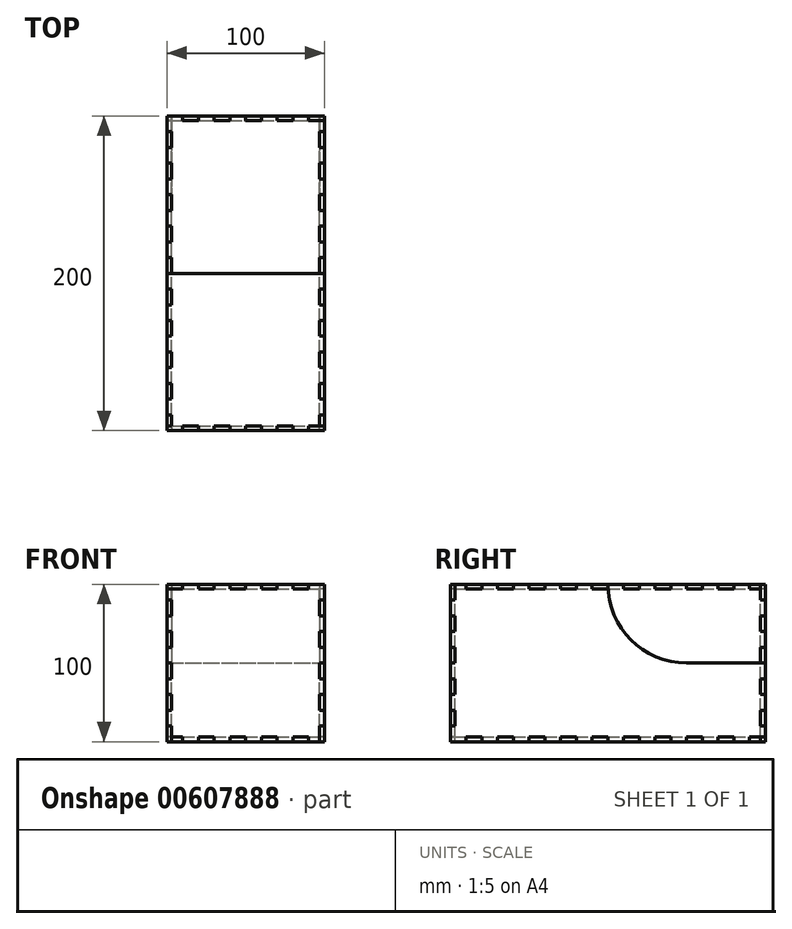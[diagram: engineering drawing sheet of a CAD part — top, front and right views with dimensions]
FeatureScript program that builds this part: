
annotation { "Feature Type Name" : "Feature", "Feature Type Description" : "" }
export const myFeature = defineFeature(function(context is Context, id is Id, definition is map)
    precondition{}
    {
        {
            var Q0;
            Q0=qCreatedBy(makeId("Right.planeOp"),FACE);
            var sketch = newSketch(context, id + "F0", { "sketchPlane" : qUnion([Q0])});
            skLineSegment(sketch, "E0.bottom", {"start": v(3, 0) * mm, "end": v(10, 0) * mm});
            skLineSegment(sketch, "E0.top", {"start": v(0, -100) * mm, "end": v(10, -100) * mm});
            skLineSegment(sketch, "E0.left", {"start": v(0, -10) * mm, "end": v(0, -20) * mm});
            skLineSegment(sketch, "E0.right", {"start": v(200, -10) * mm, "end": v(200, -20) * mm});
            skArc(sketch, "E1", {"start": v(100, 0) * mm, "mid": v(114.64, -35.36) * mm, "end": v(150, -50) * mm});
            skLineSegment(sketch, "E2", {"start": v(200, -50) * mm, "end": v(150, -50) * mm});
            skLineSegment(sketch, "E3.bottom", {"start": v(0, -90) * mm, "end": v(3, -90) * mm});
            skLineSegment(sketch, "E3.top", {"start": v(0, -80) * mm, "end": v(3, -80) * mm});
            skLineSegment(sketch, "E3.right", {"start": v(3, -90) * mm, "end": v(3, -80) * mm});
            skLineSegment(sketch, "E4.trimOffspring", {"start": v(0, -90) * mm, "end": v(0, -100) * mm});
            skLineSegment(sketch, "E5.0.1.0", {"start": v(0, -70) * mm, "end": v(3, -70) * mm});
            skLineSegment(sketch, "E5.0.1.1", {"start": v(3, -70) * mm, "end": v(3, -60) * mm});
            skLineSegment(sketch, "E5.0.1.2", {"start": v(0, -60) * mm, "end": v(3, -60) * mm});
            skLineSegment(sketch, "E5.0.2.0", {"start": v(0, -50) * mm, "end": v(3, -50) * mm});
            skLineSegment(sketch, "E5.0.2.1", {"start": v(3, -50) * mm, "end": v(3, -40) * mm});
            skLineSegment(sketch, "E5.0.2.2", {"start": v(0, -40) * mm, "end": v(3, -40) * mm});
            skLineSegment(sketch, "E5.0.3.0", {"start": v(0, -30) * mm, "end": v(3, -30) * mm});
            skLineSegment(sketch, "E5.0.3.1", {"start": v(3, -30) * mm, "end": v(3, -20) * mm});
            skLineSegment(sketch, "E5.0.3.2", {"start": v(0, -20) * mm, "end": v(3, -20) * mm});
            skLineSegment(sketch, "E5.0.4.0", {"start": v(0, -10) * mm, "end": v(3, -10) * mm});
            skLineSegment(sketch, "E5.0.4.1", {"start": v(3, -10) * mm, "end": v(3, 0) * mm});
            skLineSegment(sketch, "E5.direction1", {"start": v(0, -90) * mm, "end": v(25, -90) * mm, "construction": true});
            skLineSegment(sketch, "E5.direction2", {"start": v(0, -90) * mm, "end": v(0, -70) * mm, "construction": true});
            skLineSegment(sketch, "E6.trimOffspring", {"start": v(0, -30) * mm, "end": v(0, -40) * mm});
            skLineSegment(sketch, "E7.trimOffspring", {"start": v(0, -50) * mm, "end": v(0, -60) * mm});
            skLineSegment(sketch, "E8.trimOffspring", {"start": v(0, -70) * mm, "end": v(0, -80) * mm});
            skLineSegment(sketch, "E9.top", {"start": v(10, -97) * mm, "end": v(20, -97) * mm});
            skLineSegment(sketch, "E9.left", {"start": v(10, -100) * mm, "end": v(10, -97) * mm});
            skLineSegment(sketch, "E9.right", {"start": v(20, -100) * mm, "end": v(20, -97) * mm});
            skLineSegment(sketch, "E10.trimOffspring", {"start": v(20, -100) * mm, "end": v(30, -100) * mm});
            skLineSegment(sketch, "E11.1.0.0", {"start": v(30, -97) * mm, "end": v(40, -97) * mm});
            skLineSegment(sketch, "E11.1.0.1", {"start": v(40, -100) * mm, "end": v(40, -97) * mm});
            skLineSegment(sketch, "E11.1.0.3", {"start": v(30, -100) * mm, "end": v(30, -97) * mm});
            skLineSegment(sketch, "E11.2.0.0", {"start": v(50, -97) * mm, "end": v(60, -97) * mm});
            skLineSegment(sketch, "E11.2.0.1", {"start": v(60, -100) * mm, "end": v(60, -97) * mm});
            skLineSegment(sketch, "E11.2.0.2", {"start": v(40, -100) * mm, "end": v(50, -100) * mm});
            skLineSegment(sketch, "E11.2.0.3", {"start": v(50, -100) * mm, "end": v(50, -97) * mm});
            skLineSegment(sketch, "E11.3.0.0", {"start": v(70, -97) * mm, "end": v(80, -97) * mm});
            skLineSegment(sketch, "E11.3.0.1", {"start": v(80, -100) * mm, "end": v(80, -97) * mm});
            skLineSegment(sketch, "E11.3.0.2", {"start": v(60, -100) * mm, "end": v(70, -100) * mm});
            skLineSegment(sketch, "E11.3.0.3", {"start": v(70, -100) * mm, "end": v(70, -97) * mm});
            skLineSegment(sketch, "E11.4.0.0", {"start": v(90, -97) * mm, "end": v(100, -97) * mm});
            skLineSegment(sketch, "E11.4.0.1", {"start": v(100, -100) * mm, "end": v(100, -97) * mm});
            skLineSegment(sketch, "E11.4.0.2", {"start": v(80, -100) * mm, "end": v(90, -100) * mm});
            skLineSegment(sketch, "E11.4.0.3", {"start": v(90, -100) * mm, "end": v(90, -97) * mm});
            skLineSegment(sketch, "E11.5.0.0", {"start": v(110, -97) * mm, "end": v(120, -97) * mm});
            skLineSegment(sketch, "E11.5.0.1", {"start": v(120, -100) * mm, "end": v(120, -97) * mm});
            skLineSegment(sketch, "E11.5.0.2", {"start": v(100, -100) * mm, "end": v(110, -100) * mm});
            skLineSegment(sketch, "E11.5.0.3", {"start": v(110, -100) * mm, "end": v(110, -97) * mm});
            skLineSegment(sketch, "E11.6.0.0", {"start": v(130, -97) * mm, "end": v(140, -97) * mm});
            skLineSegment(sketch, "E11.6.0.1", {"start": v(140, -100) * mm, "end": v(140, -97) * mm});
            skLineSegment(sketch, "E11.6.0.2", {"start": v(120, -100) * mm, "end": v(130, -100) * mm});
            skLineSegment(sketch, "E11.6.0.3", {"start": v(130, -100) * mm, "end": v(130, -97) * mm});
            skLineSegment(sketch, "E11.7.0.0", {"start": v(150, -97) * mm, "end": v(160, -97) * mm});
            skLineSegment(sketch, "E11.7.0.1", {"start": v(160, -100) * mm, "end": v(160, -97) * mm});
            skLineSegment(sketch, "E11.7.0.2", {"start": v(140, -100) * mm, "end": v(150, -100) * mm});
            skLineSegment(sketch, "E11.7.0.3", {"start": v(150, -100) * mm, "end": v(150, -97) * mm});
            skLineSegment(sketch, "E11.8.0.0", {"start": v(170, -97) * mm, "end": v(180, -97) * mm});
            skLineSegment(sketch, "E11.8.0.1", {"start": v(180, -100) * mm, "end": v(180, -97) * mm});
            skLineSegment(sketch, "E11.8.0.2", {"start": v(160, -100) * mm, "end": v(170, -100) * mm});
            skLineSegment(sketch, "E11.8.0.3", {"start": v(170, -100) * mm, "end": v(170, -97) * mm});
            skLineSegment(sketch, "E11.9.0.0", {"start": v(190, -97) * mm, "end": v(200, -97) * mm});
            skLineSegment(sketch, "E11.9.0.2", {"start": v(180, -100) * mm, "end": v(190, -100) * mm});
            skLineSegment(sketch, "E11.9.0.3", {"start": v(190, -100) * mm, "end": v(190, -97) * mm});
            skLineSegment(sketch, "E11.direction1", {"start": v(0, -100) * mm, "end": v(20, -100) * mm, "construction": true});
            skLineSegment(sketch, "E12.top", {"start": v(197, -10) * mm, "end": v(200, -10) * mm});
            skLineSegment(sketch, "E12.left", {"start": v(197, -3) * mm, "end": v(197, -10) * mm});
            skLineSegment(sketch, "E13.0.1.1", {"start": v(197, -20) * mm, "end": v(197, -30) * mm});
            skLineSegment(sketch, "E13.0.1.2", {"start": v(197, -30) * mm, "end": v(200, -30) * mm});
            skLineSegment(sketch, "E13.0.1.3", {"start": v(197, -20) * mm, "end": v(200, -20) * mm});
            skLineSegment(sketch, "E13.0.2.1", {"start": v(197, -40) * mm, "end": v(197, -50) * mm});
            skLineSegment(sketch, "E13.0.2.2", {"start": v(197, -50) * mm, "end": v(200, -50) * mm});
            skLineSegment(sketch, "E13.0.2.3", {"start": v(197, -40) * mm, "end": v(200, -40) * mm});
            skLineSegment(sketch, "E13.0.3.1", {"start": v(197, -60) * mm, "end": v(197, -70) * mm});
            skLineSegment(sketch, "E13.0.3.2", {"start": v(197, -70) * mm, "end": v(200, -70) * mm});
            skLineSegment(sketch, "E13.0.3.3", {"start": v(197, -60) * mm, "end": v(200, -60) * mm});
            skLineSegment(sketch, "E13.0.4.1", {"start": v(197, -80) * mm, "end": v(197, -90) * mm});
            skLineSegment(sketch, "E13.0.4.2", {"start": v(197, -90) * mm, "end": v(200, -90) * mm});
            skLineSegment(sketch, "E13.0.4.3", {"start": v(197, -80) * mm, "end": v(200, -80) * mm});
            skLineSegment(sketch, "E13.direction1", {"start": v(197, -10) * mm, "end": v(222, -10) * mm, "construction": true});
            skLineSegment(sketch, "E13.direction2", {"start": v(197, -10) * mm, "end": v(197, -30) * mm, "construction": true});
            skLineSegment(sketch, "E14.trimOffspring", {"start": v(200, -90) * mm, "end": v(200, -97) * mm});
            skLineSegment(sketch, "E15.trimOffspring", {"start": v(200, -70) * mm, "end": v(200, -80) * mm});
            skLineSegment(sketch, "E16.trimOffspring", {"start": v(200, -50) * mm, "end": v(200, -60) * mm});
            skLineSegment(sketch, "E17.trimOffspring", {"start": v(200, -30) * mm, "end": v(200, -40) * mm});
            skLineSegment(sketch, "E18.top", {"start": v(10, -3) * mm, "end": v(20, -3) * mm});
            skLineSegment(sketch, "E18.left", {"start": v(10, 0) * mm, "end": v(10, -3) * mm});
            skLineSegment(sketch, "E18.right", {"start": v(20, 0) * mm, "end": v(20, -3) * mm});
            skLineSegment(sketch, "E19.trimOffspring", {"start": v(20, 0) * mm, "end": v(30, 0) * mm});
            skLineSegment(sketch, "E20.1.0.0", {"start": v(30, -3) * mm, "end": v(40, -3) * mm});
            skLineSegment(sketch, "E20.1.0.1", {"start": v(40, 0) * mm, "end": v(40, -3) * mm});
            skLineSegment(sketch, "E20.1.0.2", {"start": v(30, 0) * mm, "end": v(30, -3) * mm});
            skLineSegment(sketch, "E20.2.0.0", {"start": v(50, -3) * mm, "end": v(60, -3) * mm});
            skLineSegment(sketch, "E20.2.0.1", {"start": v(60, 0) * mm, "end": v(60, -3) * mm});
            skLineSegment(sketch, "E20.2.0.2", {"start": v(50, 0) * mm, "end": v(50, -3) * mm});
            skLineSegment(sketch, "E20.3.0.0", {"start": v(70, -3) * mm, "end": v(80, -3) * mm});
            skLineSegment(sketch, "E20.3.0.1", {"start": v(80, 0) * mm, "end": v(80, -3) * mm});
            skLineSegment(sketch, "E20.3.0.2", {"start": v(70, 0) * mm, "end": v(70, -3) * mm});
            skLineSegment(sketch, "E20.4.0.0", {"start": v(90, -3) * mm, "end": v(100, -3) * mm});
            skLineSegment(sketch, "E20.4.0.1", {"start": v(100, 0) * mm, "end": v(100, -3) * mm});
            skLineSegment(sketch, "E20.4.0.2", {"start": v(90, 0) * mm, "end": v(90, -3) * mm});
            skLineSegment(sketch, "E20.5.0.0", {"start": v(110, -3) * mm, "end": v(120, -3) * mm});
            skLineSegment(sketch, "E20.5.0.1", {"start": v(120, 0) * mm, "end": v(120, -3) * mm});
            skLineSegment(sketch, "E20.5.0.2", {"start": v(110, 0) * mm, "end": v(110, -3) * mm});
            skLineSegment(sketch, "E20.6.0.0", {"start": v(130, -3) * mm, "end": v(140, -3) * mm});
            skLineSegment(sketch, "E20.6.0.1", {"start": v(140, 0) * mm, "end": v(140, -3) * mm});
            skLineSegment(sketch, "E20.6.0.2", {"start": v(130, 0) * mm, "end": v(130, -3) * mm});
            skLineSegment(sketch, "E20.7.0.0", {"start": v(150, -3) * mm, "end": v(160, -3) * mm});
            skLineSegment(sketch, "E20.7.0.1", {"start": v(160, 0) * mm, "end": v(160, -3) * mm});
            skLineSegment(sketch, "E20.7.0.2", {"start": v(150, 0) * mm, "end": v(150, -3) * mm});
            skLineSegment(sketch, "E20.8.0.0", {"start": v(170, -3) * mm, "end": v(180, -3) * mm});
            skLineSegment(sketch, "E20.8.0.1", {"start": v(180, 0) * mm, "end": v(180, -3) * mm});
            skLineSegment(sketch, "E20.8.0.2", {"start": v(170, 0) * mm, "end": v(170, -3) * mm});
            skLineSegment(sketch, "E20.9.0.0", {"start": v(190, -3) * mm, "end": v(200, -3) * mm});
            skLineSegment(sketch, "E20.9.0.2", {"start": v(190, 0) * mm, "end": v(190, -3) * mm});
            skLineSegment(sketch, "E20.direction1", {"start": v(10, -3) * mm, "end": v(30, -3) * mm, "construction": true});
            skLineSegment(sketch, "E21.trimOffspring", {"start": v(40, 0) * mm, "end": v(50, 0) * mm});
            skLineSegment(sketch, "E22.trimOffspring", {"start": v(60, 0) * mm, "end": v(70, 0) * mm});
            skLineSegment(sketch, "E23.trimOffspring", {"start": v(80, 0) * mm, "end": v(90, 0) * mm});
            skLineSegment(sketch, "E24.trimOffspring", {"start": v(100, 0) * mm, "end": v(110, 0) * mm});
            skLineSegment(sketch, "E25.trimOffspring", {"start": v(120, 0) * mm, "end": v(130, 0) * mm});
            skLineSegment(sketch, "E26.trimOffspring", {"start": v(140, 0) * mm, "end": v(150, 0) * mm});
            skLineSegment(sketch, "E27.trimOffspring", {"start": v(160, 0) * mm, "end": v(170, 0) * mm});
            skLineSegment(sketch, "E28.trimOffspring", {"start": v(180, 0) * mm, "end": v(190, 0) * mm});
            skSolve(sketch);
        }
        {
            var Q0;
            Q0=makeQuery(id+"F0.imprint","IMPRINT",FACE,{"disambiguationData":[TD([[makeQuery(id+"F0.imprint","IMPRINT",EDGE,{"derivedFrom":sQuery(id+"F0.wireOp",EDGE,"E0.bottom")}),-1.0]])]});
            extrude(context, id + "F1", {"entities" : qUnion([Q0]), "depth" : 3 * mm, "offsetDistance" : 25 * mm});
        }
        {
            var Q0;
            Q0=makeQuery(id+"F0.imprint","IMPRINT",FACE,{"disambiguationData":[TD([[makeQuery(id+"F0.imprint","IMPRINT",EDGE,{"derivedFrom":sQuery(id+"F0.wireOp",EDGE,"E0.right")}),-1.0]])]});
            extrude(context, id + "F2", {"entities" : qUnion([Q0]), "depth" : 3 * mm, "offsetDistance" : 25 * mm});
        }
        {
            var Q0;
            Q0=qCreatedBy(makeId("Front.planeOp"),FACE);
            var sketch = newSketch(context, id + "F3", { "sketchPlane" : qUnion([Q0])});
            skLineSegment(sketch, "E29.bottom", {"start": v(3, 0) * mm, "end": v(-7, 0) * mm});
            skLineSegment(sketch, "E29.top", {"start": v(3, -100) * mm, "end": v(-7, -100) * mm});
            skLineSegment(sketch, "E29.left", {"start": v(3, 0) * mm, "end": v(3, -100) * mm});
            skLineSegment(sketch, "E29.right", {"start": v(-97, -3) * mm, "end": v(-97, -100) * mm});
            skLineSegment(sketch, "E30.top", {"start": v(-97, -3) * mm, "end": v(-87, -3) * mm});
            skLineSegment(sketch, "E30.right", {"start": v(-87, 0) * mm, "end": v(-87, -3) * mm});
            skLineSegment(sketch, "E31.top", {"start": v(-97, -97) * mm, "end": v(-87, -97) * mm});
            skLineSegment(sketch, "E31.left", {"start": v(-97, -100) * mm, "end": v(-97, -97) * mm});
            skLineSegment(sketch, "E31.right", {"start": v(-87, -100) * mm, "end": v(-87, -97) * mm});
            skLineSegment(sketch, "E32.1.0.0", {"start": v(-67, 0) * mm, "end": v(-67, -3) * mm});
            skLineSegment(sketch, "E32.1.0.1", {"start": v(-77, 0) * mm, "end": v(-77, -3) * mm});
            skLineSegment(sketch, "E32.1.0.2", {"start": v(-77, -3) * mm, "end": v(-67, -3) * mm});
            skLineSegment(sketch, "E32.2.0.0", {"start": v(-47, 0) * mm, "end": v(-47, -3) * mm});
            skLineSegment(sketch, "E32.2.0.1", {"start": v(-57, 0) * mm, "end": v(-57, -3) * mm});
            skLineSegment(sketch, "E32.2.0.2", {"start": v(-57, -3) * mm, "end": v(-47, -3) * mm});
            skLineSegment(sketch, "E32.3.0.0", {"start": v(-27, 0) * mm, "end": v(-27, -3) * mm});
            skLineSegment(sketch, "E32.3.0.1", {"start": v(-37, 0) * mm, "end": v(-37, -3) * mm});
            skLineSegment(sketch, "E32.3.0.2", {"start": v(-37, -3) * mm, "end": v(-27, -3) * mm});
            skLineSegment(sketch, "E32.4.0.0", {"start": v(-7, 0) * mm, "end": v(-7, -3) * mm});
            skLineSegment(sketch, "E32.4.0.1", {"start": v(-17, 0) * mm, "end": v(-17, -3) * mm});
            skLineSegment(sketch, "E32.4.0.2", {"start": v(-17, -3) * mm, "end": v(-7, -3) * mm});
            skLineSegment(sketch, "E32.direction1", {"start": v(-97, -3) * mm, "end": v(-77, -3) * mm, "construction": true});
            skLineSegment(sketch, "E33.1.0.1", {"start": v(-77, -97) * mm, "end": v(-67, -97) * mm});
            skLineSegment(sketch, "E33.1.0.2", {"start": v(-77, -100) * mm, "end": v(-77, -97) * mm});
            skLineSegment(sketch, "E33.1.0.3", {"start": v(-67, -100) * mm, "end": v(-67, -97) * mm});
            skLineSegment(sketch, "E33.2.0.1", {"start": v(-57, -97) * mm, "end": v(-47, -97) * mm});
            skLineSegment(sketch, "E33.2.0.2", {"start": v(-57, -100) * mm, "end": v(-57, -97) * mm});
            skLineSegment(sketch, "E33.2.0.3", {"start": v(-47, -100) * mm, "end": v(-47, -97) * mm});
            skLineSegment(sketch, "E33.3.0.1", {"start": v(-37, -97) * mm, "end": v(-27, -97) * mm});
            skLineSegment(sketch, "E33.3.0.2", {"start": v(-37, -100) * mm, "end": v(-37, -97) * mm});
            skLineSegment(sketch, "E33.3.0.3", {"start": v(-27, -100) * mm, "end": v(-27, -97) * mm});
            skLineSegment(sketch, "E33.4.0.1", {"start": v(-17, -97) * mm, "end": v(-7, -97) * mm});
            skLineSegment(sketch, "E33.4.0.2", {"start": v(-17, -100) * mm, "end": v(-17, -97) * mm});
            skLineSegment(sketch, "E33.4.0.3", {"start": v(-7, -100) * mm, "end": v(-7, -97) * mm});
            skLineSegment(sketch, "E33.direction1", {"start": v(-87, -100) * mm, "end": v(-77, -100) * mm, "construction": true});
            skLineSegment(sketch, "E34.trimOffspring", {"start": v(-77, 0) * mm, "end": v(-87, 0) * mm});
            skLineSegment(sketch, "E35.trimOffspring", {"start": v(-57, 0) * mm, "end": v(-67, 0) * mm});
            skLineSegment(sketch, "E36.trimOffspring", {"start": v(-37, 0) * mm, "end": v(-47, 0) * mm});
            skLineSegment(sketch, "E37.trimOffspring", {"start": v(-17, 0) * mm, "end": v(-27, 0) * mm});
            skLineSegment(sketch, "E38.trimOffspring", {"start": v(-17, -100) * mm, "end": v(-27, -100) * mm});
            skLineSegment(sketch, "E39.trimOffspring", {"start": v(-37, -100) * mm, "end": v(-47, -100) * mm});
            skLineSegment(sketch, "E40.trimOffspring", {"start": v(-57, -100) * mm, "end": v(-67, -100) * mm});
            skLineSegment(sketch, "E41.trimOffspring", {"start": v(-77, -100) * mm, "end": v(-87, -100) * mm});
            skLineSegment(sketch, "E42", {"start": v(-97, -50) * mm, "end": v(3, -50) * mm});
            skSolve(sketch);
        }
        {
            var Q0;
            Q0=makeQuery(id+"F1.opExtrude","SWEPT_BODY",BODY,{"disambiguationData":[OSD([sQuery(id+"F0.wireOp",EDGE,"E0.bottom"),sQuery(id+"F0.wireOp",EDGE,"E0.top"),sQuery(id+"F0.wireOp",EDGE,"E0.left"),sQuery(id+"F0.wireOp",EDGE,"E1"),sQuery(id+"F0.wireOp",EDGE,"E2"),sQuery(id+"F0.wireOp",EDGE,"E3.bottom"),sQuery(id+"F0.wireOp",EDGE,"E3.top"),sQuery(id+"F0.wireOp",EDGE,"E3.right"),sQuery(id+"F0.wireOp",EDGE,"E4.trimOffspring"),sQuery(id+"F0.wireOp",EDGE,"E5.0.1.0"),sQuery(id+"F0.wireOp",EDGE,"E5.0.1.1"),sQuery(id+"F0.wireOp",EDGE,"E5.0.1.2"),sQuery(id+"F0.wireOp",EDGE,"E5.0.2.0"),sQuery(id+"F0.wireOp",EDGE,"E5.0.2.1"),sQuery(id+"F0.wireOp",EDGE,"E5.0.2.2"),sQuery(id+"F0.wireOp",EDGE,"E5.0.3.0"),sQuery(id+"F0.wireOp",EDGE,"E5.0.3.1"),sQuery(id+"F0.wireOp",EDGE,"E5.0.3.2"),sQuery(id+"F0.wireOp",EDGE,"E5.0.4.0"),sQuery(id+"F0.wireOp",EDGE,"E5.0.4.1"),sQuery(id+"F0.wireOp",EDGE,"E6.trimOffspring"),sQuery(id+"F0.wireOp",EDGE,"E7.trimOffspring"),sQuery(id+"F0.wireOp",EDGE,"E8.trimOffspring"),sQuery(id+"F0.wireOp",EDGE,"E9.top"),sQuery(id+"F0.wireOp",EDGE,"E9.left"),sQuery(id+"F0.wireOp",EDGE,"E9.right"),sQuery(id+"F0.wireOp",EDGE,"E11.1.0.0"),sQuery(id+"F0.wireOp",EDGE,"E11.1.0.1"),sQuery(id+"F0.wireOp",EDGE,"E10.trimOffspring"),sQuery(id+"F0.wireOp",EDGE,"E11.1.0.3"),sQuery(id+"F0.wireOp",EDGE,"E11.2.0.0"),sQuery(id+"F0.wireOp",EDGE,"E11.2.0.1"),sQuery(id+"F0.wireOp",EDGE,"E11.2.0.3"),sQuery(id+"F0.wireOp",EDGE,"E11.3.0.0"),sQuery(id+"F0.wireOp",EDGE,"E11.3.0.1"),sQuery(id+"F0.wireOp",EDGE,"E11.3.0.3"),sQuery(id+"F0.wireOp",EDGE,"E11.4.0.0"),sQuery(id+"F0.wireOp",EDGE,"E11.4.0.1"),sQuery(id+"F0.wireOp",EDGE,"E11.4.0.3"),sQuery(id+"F0.wireOp",EDGE,"E11.5.0.0"),sQuery(id+"F0.wireOp",EDGE,"E11.5.0.1"),sQuery(id+"F0.wireOp",EDGE,"E11.5.0.3"),sQuery(id+"F0.wireOp",EDGE,"E11.6.0.0"),sQuery(id+"F0.wireOp",EDGE,"E11.6.0.1"),sQuery(id+"F0.wireOp",EDGE,"E11.6.0.3"),sQuery(id+"F0.wireOp",EDGE,"E11.7.0.0"),sQuery(id+"F0.wireOp",EDGE,"E11.7.0.1"),sQuery(id+"F0.wireOp",EDGE,"E11.7.0.3"),sQuery(id+"F0.wireOp",EDGE,"E11.8.0.0"),sQuery(id+"F0.wireOp",EDGE,"E11.8.0.1"),sQuery(id+"F0.wireOp",EDGE,"E11.8.0.3"),sQuery(id+"F0.wireOp",EDGE,"E11.9.0.0"),sQuery(id+"F0.wireOp",EDGE,"E11.9.0.3"),sQuery(id+"F0.wireOp",EDGE,"E11.2.0.2"),sQuery(id+"F0.wireOp",EDGE,"E11.3.0.2"),sQuery(id+"F0.wireOp",EDGE,"E11.4.0.2"),sQuery(id+"F0.wireOp",EDGE,"E11.5.0.2"),sQuery(id+"F0.wireOp",EDGE,"E11.6.0.2"),sQuery(id+"F0.wireOp",EDGE,"E11.7.0.2"),sQuery(id+"F0.wireOp",EDGE,"E11.8.0.2"),sQuery(id+"F0.wireOp",EDGE,"E11.9.0.2"),sQuery(id+"F0.wireOp",EDGE,"E13.0.2.2"),sQuery(id+"F0.wireOp",EDGE,"E13.0.3.1"),sQuery(id+"F0.wireOp",EDGE,"E13.0.3.2"),sQuery(id+"F0.wireOp",EDGE,"E13.0.3.3"),sQuery(id+"F0.wireOp",EDGE,"E13.0.4.1"),sQuery(id+"F0.wireOp",EDGE,"E13.0.4.2"),sQuery(id+"F0.wireOp",EDGE,"E13.0.4.3"),sQuery(id+"F0.wireOp",EDGE,"E14.trimOffspring"),sQuery(id+"F0.wireOp",EDGE,"E15.trimOffspring"),sQuery(id+"F0.wireOp",EDGE,"E16.trimOffspring"),sQuery(id+"F0.wireOp",EDGE,"E18.top"),sQuery(id+"F0.wireOp",EDGE,"E18.left"),sQuery(id+"F0.wireOp",EDGE,"E18.right"),sQuery(id+"F0.wireOp",EDGE,"E19.trimOffspring"),sQuery(id+"F0.wireOp",EDGE,"E20.1.0.0"),sQuery(id+"F0.wireOp",EDGE,"E20.1.0.1"),sQuery(id+"F0.wireOp",EDGE,"E20.1.0.2"),sQuery(id+"F0.wireOp",EDGE,"E20.2.0.0"),sQuery(id+"F0.wireOp",EDGE,"E20.2.0.1"),sQuery(id+"F0.wireOp",EDGE,"E20.2.0.2"),sQuery(id+"F0.wireOp",EDGE,"E20.3.0.0"),sQuery(id+"F0.wireOp",EDGE,"E20.3.0.1"),sQuery(id+"F0.wireOp",EDGE,"E20.3.0.2"),sQuery(id+"F0.wireOp",EDGE,"E20.4.0.0"),sQuery(id+"F0.wireOp",EDGE,"E20.4.0.1"),sQuery(id+"F0.wireOp",EDGE,"E20.4.0.2"),sQuery(id+"F0.wireOp",EDGE,"E21.trimOffspring"),sQuery(id+"F0.wireOp",EDGE,"E22.trimOffspring"),sQuery(id+"F0.wireOp",EDGE,"E23.trimOffspring")])]});
            transform(context, id + "F4", {"entities" : qUnion([Q0]), "transformType" : TransformType.TRANSLATION_3D, "dx" : -97 * mm, "dy" : 0 * mm, "dz" : 0 * mm, "makeCopy" : true});
        }
        {
            var Q0;
            Q0=makeQuery(id+"F2.opExtrude","SWEPT_BODY",BODY,{"disambiguationData":[OSD([sQuery(id+"F0.wireOp",EDGE,"E0.right"),sQuery(id+"F0.wireOp",EDGE,"E1"),sQuery(id+"F0.wireOp",EDGE,"E2"),sQuery(id+"F0.wireOp",EDGE,"E12.top"),sQuery(id+"F0.wireOp",EDGE,"E12.left"),sQuery(id+"F0.wireOp",EDGE,"E13.0.1.1"),sQuery(id+"F0.wireOp",EDGE,"E13.0.1.2"),sQuery(id+"F0.wireOp",EDGE,"E13.0.1.3"),sQuery(id+"F0.wireOp",EDGE,"E13.0.2.1"),sQuery(id+"F0.wireOp",EDGE,"E13.0.2.3"),sQuery(id+"F0.wireOp",EDGE,"E17.trimOffspring"),sQuery(id+"F0.wireOp",EDGE,"E20.5.0.0"),sQuery(id+"F0.wireOp",EDGE,"E20.5.0.1"),sQuery(id+"F0.wireOp",EDGE,"E20.5.0.2"),sQuery(id+"F0.wireOp",EDGE,"E20.6.0.0"),sQuery(id+"F0.wireOp",EDGE,"E20.6.0.1"),sQuery(id+"F0.wireOp",EDGE,"E20.6.0.2"),sQuery(id+"F0.wireOp",EDGE,"E20.7.0.0"),sQuery(id+"F0.wireOp",EDGE,"E20.7.0.1"),sQuery(id+"F0.wireOp",EDGE,"E20.7.0.2"),sQuery(id+"F0.wireOp",EDGE,"E20.8.0.0"),sQuery(id+"F0.wireOp",EDGE,"E20.8.0.1"),sQuery(id+"F0.wireOp",EDGE,"E20.8.0.2"),sQuery(id+"F0.wireOp",EDGE,"E20.9.0.0"),sQuery(id+"F0.wireOp",EDGE,"E20.9.0.2"),sQuery(id+"F0.wireOp",EDGE,"E24.trimOffspring"),sQuery(id+"F0.wireOp",EDGE,"E25.trimOffspring"),sQuery(id+"F0.wireOp",EDGE,"E26.trimOffspring"),sQuery(id+"F0.wireOp",EDGE,"E27.trimOffspring"),sQuery(id+"F0.wireOp",EDGE,"E28.trimOffspring")])]});
            transform(context, id + "F5", {"entities" : qUnion([Q0]), "transformType" : TransformType.TRANSLATION_3D, "dx" : -97 * mm, "dy" : 0 * mm, "dz" : 0 * mm, "makeCopy" : true});
        }
        {
            var Q0;
            Q0 = qSketchRegion(id + "F3", true);
            extrude(context, id + "F6", {"entities" : qUnion([Q0]), "depth" : -3 * mm, "offsetDistance" : 25 * mm});
        }
        {
            var Q0;
            Q0=makeQuery(id+"F4.opPattern","COPY",BODY,{"derivedFrom":makeQuery(id+"F1.opExtrude","SWEPT_BODY",BODY,{"disambiguationData":[OSD([sQuery(id+"F0.wireOp",EDGE,"E0.bottom"),sQuery(id+"F0.wireOp",EDGE,"E0.top"),sQuery(id+"F0.wireOp",EDGE,"E0.left"),sQuery(id+"F0.wireOp",EDGE,"E1"),sQuery(id+"F0.wireOp",EDGE,"E2"),sQuery(id+"F0.wireOp",EDGE,"E3.bottom"),sQuery(id+"F0.wireOp",EDGE,"E3.top"),sQuery(id+"F0.wireOp",EDGE,"E3.right"),sQuery(id+"F0.wireOp",EDGE,"E4.trimOffspring"),sQuery(id+"F0.wireOp",EDGE,"E5.0.1.0"),sQuery(id+"F0.wireOp",EDGE,"E5.0.1.1"),sQuery(id+"F0.wireOp",EDGE,"E5.0.1.2"),sQuery(id+"F0.wireOp",EDGE,"E5.0.2.0"),sQuery(id+"F0.wireOp",EDGE,"E5.0.2.1"),sQuery(id+"F0.wireOp",EDGE,"E5.0.2.2"),sQuery(id+"F0.wireOp",EDGE,"E5.0.3.0"),sQuery(id+"F0.wireOp",EDGE,"E5.0.3.1"),sQuery(id+"F0.wireOp",EDGE,"E5.0.3.2"),sQuery(id+"F0.wireOp",EDGE,"E5.0.4.0"),sQuery(id+"F0.wireOp",EDGE,"E5.0.4.1"),sQuery(id+"F0.wireOp",EDGE,"E6.trimOffspring"),sQuery(id+"F0.wireOp",EDGE,"E7.trimOffspring"),sQuery(id+"F0.wireOp",EDGE,"E8.trimOffspring"),sQuery(id+"F0.wireOp",EDGE,"E9.top"),sQuery(id+"F0.wireOp",EDGE,"E9.left"),sQuery(id+"F0.wireOp",EDGE,"E9.right"),sQuery(id+"F0.wireOp",EDGE,"E11.1.0.0"),sQuery(id+"F0.wireOp",EDGE,"E11.1.0.1"),sQuery(id+"F0.wireOp",EDGE,"E10.trimOffspring"),sQuery(id+"F0.wireOp",EDGE,"E11.1.0.3"),sQuery(id+"F0.wireOp",EDGE,"E11.2.0.0"),sQuery(id+"F0.wireOp",EDGE,"E11.2.0.1"),sQuery(id+"F0.wireOp",EDGE,"E11.2.0.3"),sQuery(id+"F0.wireOp",EDGE,"E11.3.0.0"),sQuery(id+"F0.wireOp",EDGE,"E11.3.0.1"),sQuery(id+"F0.wireOp",EDGE,"E11.3.0.3"),sQuery(id+"F0.wireOp",EDGE,"E11.4.0.0"),sQuery(id+"F0.wireOp",EDGE,"E11.4.0.1"),sQuery(id+"F0.wireOp",EDGE,"E11.4.0.3"),sQuery(id+"F0.wireOp",EDGE,"E11.5.0.0"),sQuery(id+"F0.wireOp",EDGE,"E11.5.0.1"),sQuery(id+"F0.wireOp",EDGE,"E11.5.0.3"),sQuery(id+"F0.wireOp",EDGE,"E11.6.0.0"),sQuery(id+"F0.wireOp",EDGE,"E11.6.0.1"),sQuery(id+"F0.wireOp",EDGE,"E11.6.0.3"),sQuery(id+"F0.wireOp",EDGE,"E11.7.0.0"),sQuery(id+"F0.wireOp",EDGE,"E11.7.0.1"),sQuery(id+"F0.wireOp",EDGE,"E11.7.0.3"),sQuery(id+"F0.wireOp",EDGE,"E11.8.0.0"),sQuery(id+"F0.wireOp",EDGE,"E11.8.0.1"),sQuery(id+"F0.wireOp",EDGE,"E11.8.0.3"),sQuery(id+"F0.wireOp",EDGE,"E11.9.0.0"),sQuery(id+"F0.wireOp",EDGE,"E11.9.0.3"),sQuery(id+"F0.wireOp",EDGE,"E11.2.0.2"),sQuery(id+"F0.wireOp",EDGE,"E11.3.0.2"),sQuery(id+"F0.wireOp",EDGE,"E11.4.0.2"),sQuery(id+"F0.wireOp",EDGE,"E11.5.0.2"),sQuery(id+"F0.wireOp",EDGE,"E11.6.0.2"),sQuery(id+"F0.wireOp",EDGE,"E11.7.0.2"),sQuery(id+"F0.wireOp",EDGE,"E11.8.0.2"),sQuery(id+"F0.wireOp",EDGE,"E11.9.0.2"),sQuery(id+"F0.wireOp",EDGE,"E13.0.2.2"),sQuery(id+"F0.wireOp",EDGE,"E13.0.3.1"),sQuery(id+"F0.wireOp",EDGE,"E13.0.3.2"),sQuery(id+"F0.wireOp",EDGE,"E13.0.3.3"),sQuery(id+"F0.wireOp",EDGE,"E13.0.4.1"),sQuery(id+"F0.wireOp",EDGE,"E13.0.4.2"),sQuery(id+"F0.wireOp",EDGE,"E13.0.4.3"),sQuery(id+"F0.wireOp",EDGE,"E14.trimOffspring"),sQuery(id+"F0.wireOp",EDGE,"E15.trimOffspring"),sQuery(id+"F0.wireOp",EDGE,"E16.trimOffspring"),sQuery(id+"F0.wireOp",EDGE,"E18.top"),sQuery(id+"F0.wireOp",EDGE,"E18.left"),sQuery(id+"F0.wireOp",EDGE,"E18.right"),sQuery(id+"F0.wireOp",EDGE,"E19.trimOffspring"),sQuery(id+"F0.wireOp",EDGE,"E20.1.0.0"),sQuery(id+"F0.wireOp",EDGE,"E20.1.0.1"),sQuery(id+"F0.wireOp",EDGE,"E20.1.0.2"),sQuery(id+"F0.wireOp",EDGE,"E20.2.0.0"),sQuery(id+"F0.wireOp",EDGE,"E20.2.0.1"),sQuery(id+"F0.wireOp",EDGE,"E20.2.0.2"),sQuery(id+"F0.wireOp",EDGE,"E20.3.0.0"),sQuery(id+"F0.wireOp",EDGE,"E20.3.0.1"),sQuery(id+"F0.wireOp",EDGE,"E20.3.0.2"),sQuery(id+"F0.wireOp",EDGE,"E20.4.0.0"),sQuery(id+"F0.wireOp",EDGE,"E20.4.0.1"),sQuery(id+"F0.wireOp",EDGE,"E20.4.0.2"),sQuery(id+"F0.wireOp",EDGE,"E21.trimOffspring"),sQuery(id+"F0.wireOp",EDGE,"E22.trimOffspring"),sQuery(id+"F0.wireOp",EDGE,"E23.trimOffspring")])]}),"instanceName":"1"});
            var Q1;
            Q1=makeQuery(id+"F1.opExtrude","SWEPT_BODY",BODY,{"disambiguationData":[OSD([sQuery(id+"F0.wireOp",EDGE,"E0.bottom"),sQuery(id+"F0.wireOp",EDGE,"E0.top"),sQuery(id+"F0.wireOp",EDGE,"E0.left"),sQuery(id+"F0.wireOp",EDGE,"E1"),sQuery(id+"F0.wireOp",EDGE,"E2"),sQuery(id+"F0.wireOp",EDGE,"E3.bottom"),sQuery(id+"F0.wireOp",EDGE,"E3.top"),sQuery(id+"F0.wireOp",EDGE,"E3.right"),sQuery(id+"F0.wireOp",EDGE,"E4.trimOffspring"),sQuery(id+"F0.wireOp",EDGE,"E5.0.1.0"),sQuery(id+"F0.wireOp",EDGE,"E5.0.1.1"),sQuery(id+"F0.wireOp",EDGE,"E5.0.1.2"),sQuery(id+"F0.wireOp",EDGE,"E5.0.2.0"),sQuery(id+"F0.wireOp",EDGE,"E5.0.2.1"),sQuery(id+"F0.wireOp",EDGE,"E5.0.2.2"),sQuery(id+"F0.wireOp",EDGE,"E5.0.3.0"),sQuery(id+"F0.wireOp",EDGE,"E5.0.3.1"),sQuery(id+"F0.wireOp",EDGE,"E5.0.3.2"),sQuery(id+"F0.wireOp",EDGE,"E5.0.4.0"),sQuery(id+"F0.wireOp",EDGE,"E5.0.4.1"),sQuery(id+"F0.wireOp",EDGE,"E6.trimOffspring"),sQuery(id+"F0.wireOp",EDGE,"E7.trimOffspring"),sQuery(id+"F0.wireOp",EDGE,"E8.trimOffspring"),sQuery(id+"F0.wireOp",EDGE,"E9.top"),sQuery(id+"F0.wireOp",EDGE,"E9.left"),sQuery(id+"F0.wireOp",EDGE,"E9.right"),sQuery(id+"F0.wireOp",EDGE,"E11.1.0.0"),sQuery(id+"F0.wireOp",EDGE,"E11.1.0.1"),sQuery(id+"F0.wireOp",EDGE,"E10.trimOffspring"),sQuery(id+"F0.wireOp",EDGE,"E11.1.0.3"),sQuery(id+"F0.wireOp",EDGE,"E11.2.0.0"),sQuery(id+"F0.wireOp",EDGE,"E11.2.0.1"),sQuery(id+"F0.wireOp",EDGE,"E11.2.0.3"),sQuery(id+"F0.wireOp",EDGE,"E11.3.0.0"),sQuery(id+"F0.wireOp",EDGE,"E11.3.0.1"),sQuery(id+"F0.wireOp",EDGE,"E11.3.0.3"),sQuery(id+"F0.wireOp",EDGE,"E11.4.0.0"),sQuery(id+"F0.wireOp",EDGE,"E11.4.0.1"),sQuery(id+"F0.wireOp",EDGE,"E11.4.0.3"),sQuery(id+"F0.wireOp",EDGE,"E11.5.0.0"),sQuery(id+"F0.wireOp",EDGE,"E11.5.0.1"),sQuery(id+"F0.wireOp",EDGE,"E11.5.0.3"),sQuery(id+"F0.wireOp",EDGE,"E11.6.0.0"),sQuery(id+"F0.wireOp",EDGE,"E11.6.0.1"),sQuery(id+"F0.wireOp",EDGE,"E11.6.0.3"),sQuery(id+"F0.wireOp",EDGE,"E11.7.0.0"),sQuery(id+"F0.wireOp",EDGE,"E11.7.0.1"),sQuery(id+"F0.wireOp",EDGE,"E11.7.0.3"),sQuery(id+"F0.wireOp",EDGE,"E11.8.0.0"),sQuery(id+"F0.wireOp",EDGE,"E11.8.0.1"),sQuery(id+"F0.wireOp",EDGE,"E11.8.0.3"),sQuery(id+"F0.wireOp",EDGE,"E11.9.0.0"),sQuery(id+"F0.wireOp",EDGE,"E11.9.0.3"),sQuery(id+"F0.wireOp",EDGE,"E11.2.0.2"),sQuery(id+"F0.wireOp",EDGE,"E11.3.0.2"),sQuery(id+"F0.wireOp",EDGE,"E11.4.0.2"),sQuery(id+"F0.wireOp",EDGE,"E11.5.0.2"),sQuery(id+"F0.wireOp",EDGE,"E11.6.0.2"),sQuery(id+"F0.wireOp",EDGE,"E11.7.0.2"),sQuery(id+"F0.wireOp",EDGE,"E11.8.0.2"),sQuery(id+"F0.wireOp",EDGE,"E11.9.0.2"),sQuery(id+"F0.wireOp",EDGE,"E13.0.2.2"),sQuery(id+"F0.wireOp",EDGE,"E13.0.3.1"),sQuery(id+"F0.wireOp",EDGE,"E13.0.3.2"),sQuery(id+"F0.wireOp",EDGE,"E13.0.3.3"),sQuery(id+"F0.wireOp",EDGE,"E13.0.4.1"),sQuery(id+"F0.wireOp",EDGE,"E13.0.4.2"),sQuery(id+"F0.wireOp",EDGE,"E13.0.4.3"),sQuery(id+"F0.wireOp",EDGE,"E14.trimOffspring"),sQuery(id+"F0.wireOp",EDGE,"E15.trimOffspring"),sQuery(id+"F0.wireOp",EDGE,"E16.trimOffspring"),sQuery(id+"F0.wireOp",EDGE,"E18.top"),sQuery(id+"F0.wireOp",EDGE,"E18.left"),sQuery(id+"F0.wireOp",EDGE,"E18.right"),sQuery(id+"F0.wireOp",EDGE,"E19.trimOffspring"),sQuery(id+"F0.wireOp",EDGE,"E20.1.0.0"),sQuery(id+"F0.wireOp",EDGE,"E20.1.0.1"),sQuery(id+"F0.wireOp",EDGE,"E20.1.0.2"),sQuery(id+"F0.wireOp",EDGE,"E20.2.0.0"),sQuery(id+"F0.wireOp",EDGE,"E20.2.0.1"),sQuery(id+"F0.wireOp",EDGE,"E20.2.0.2"),sQuery(id+"F0.wireOp",EDGE,"E20.3.0.0"),sQuery(id+"F0.wireOp",EDGE,"E20.3.0.1"),sQuery(id+"F0.wireOp",EDGE,"E20.3.0.2"),sQuery(id+"F0.wireOp",EDGE,"E20.4.0.0"),sQuery(id+"F0.wireOp",EDGE,"E20.4.0.1"),sQuery(id+"F0.wireOp",EDGE,"E20.4.0.2"),sQuery(id+"F0.wireOp",EDGE,"E21.trimOffspring"),sQuery(id+"F0.wireOp",EDGE,"E22.trimOffspring"),sQuery(id+"F0.wireOp",EDGE,"E23.trimOffspring")])]});
            var Q2;
            Q2=makeQuery(id+"F6.opExtrude","SWEPT_BODY",BODY,{"disambiguationData":[OSD([sQuery(id+"F3.wireOp",EDGE,"E29.bottom"),sQuery(id+"F3.wireOp",EDGE,"E29.top"),sQuery(id+"F3.wireOp",EDGE,"E29.left"),sQuery(id+"F3.wireOp",EDGE,"E29.right"),sQuery(id+"F3.wireOp",EDGE,"E30.top"),sQuery(id+"F3.wireOp",EDGE,"E30.right"),sQuery(id+"F3.wireOp",EDGE,"E31.top"),sQuery(id+"F3.wireOp",EDGE,"E31.right"),sQuery(id+"F3.wireOp",EDGE,"E32.1.0.0"),sQuery(id+"F3.wireOp",EDGE,"E32.1.0.1"),sQuery(id+"F3.wireOp",EDGE,"E32.1.0.2"),sQuery(id+"F3.wireOp",EDGE,"E32.2.0.0"),sQuery(id+"F3.wireOp",EDGE,"E32.2.0.1"),sQuery(id+"F3.wireOp",EDGE,"E32.2.0.2"),sQuery(id+"F3.wireOp",EDGE,"E32.3.0.0"),sQuery(id+"F3.wireOp",EDGE,"E32.3.0.1"),sQuery(id+"F3.wireOp",EDGE,"E32.3.0.2"),sQuery(id+"F3.wireOp",EDGE,"E32.4.0.0"),sQuery(id+"F3.wireOp",EDGE,"E32.4.0.1"),sQuery(id+"F3.wireOp",EDGE,"E32.4.0.2"),sQuery(id+"F3.wireOp",EDGE,"E33.1.0.1"),sQuery(id+"F3.wireOp",EDGE,"E33.1.0.2"),sQuery(id+"F3.wireOp",EDGE,"E33.1.0.3"),sQuery(id+"F3.wireOp",EDGE,"E33.2.0.1"),sQuery(id+"F3.wireOp",EDGE,"E33.2.0.2"),sQuery(id+"F3.wireOp",EDGE,"E33.2.0.3"),sQuery(id+"F3.wireOp",EDGE,"E33.3.0.1"),sQuery(id+"F3.wireOp",EDGE,"E33.3.0.2"),sQuery(id+"F3.wireOp",EDGE,"E33.3.0.3"),sQuery(id+"F3.wireOp",EDGE,"E33.4.0.1"),sQuery(id+"F3.wireOp",EDGE,"E33.4.0.2"),sQuery(id+"F3.wireOp",EDGE,"E33.4.0.3"),sQuery(id+"F3.wireOp",EDGE,"E34.trimOffspring"),sQuery(id+"F3.wireOp",EDGE,"E35.trimOffspring"),sQuery(id+"F3.wireOp",EDGE,"E36.trimOffspring"),sQuery(id+"F3.wireOp",EDGE,"E37.trimOffspring"),sQuery(id+"F3.wireOp",EDGE,"E38.trimOffspring"),sQuery(id+"F3.wireOp",EDGE,"E39.trimOffspring"),sQuery(id+"F3.wireOp",EDGE,"E40.trimOffspring"),sQuery(id+"F3.wireOp",EDGE,"E41.trimOffspring")])]});
            booleanBodies(context, id + "F7", {"operationType" : BooleanOperationType.SUBTRACTION, "tools" : qUnion([Q0, Q1]), "targets" : qUnion([Q2]), "keepTools" : true});
        }
        {
            var Q0;
            {var subQ1=sQuery(id+"F3.wireOp",EDGE,"E29.top");Q0=makeQuery(id+"F3.imprint","IMPRINT",FACE,{"disambiguationData":[TD([[makeQuery(id+"F3.imprint","IMPRINT",EDGE,{"derivedFrom":subQ1}),-1.0]])]});}
            extrude(context, id + "F8", {"entities" : qUnion([Q0]), "oppositeDirection" : true, "depth" : 200 * mm, "offsetDistance" : 25 * mm, "hasSecondDirection" : true, "secondDirectionOppositeDirection" : true, "secondDirectionDepth" : 197 * mm});
        }
        {
            var Q0;
            {var subQ0=sQuery(id+"F3.wireOp",EDGE,"E29.bottom");Q0=makeQuery(id+"F3.imprint","IMPRINT",FACE,{"disambiguationData":[TD([[makeQuery(id+"F3.imprint","IMPRINT",EDGE,{"derivedFrom":subQ0}),1.0]])]});}
            extrude(context, id + "F9", {"entities" : qUnion([Q0]), "oppositeDirection" : true, "depth" : 200 * mm, "offsetDistance" : 25 * mm, "hasSecondDirection" : true, "secondDirectionOppositeDirection" : true, "secondDirectionDepth" : 197 * mm});
        }
        {
            var Q0;
            Q0=makeQuery(id+"F2.opExtrude","SWEPT_BODY",BODY,{"disambiguationData":[OSD([sQuery(id+"F0.wireOp",EDGE,"E0.right"),sQuery(id+"F0.wireOp",EDGE,"E1"),sQuery(id+"F0.wireOp",EDGE,"E2"),sQuery(id+"F0.wireOp",EDGE,"E12.top"),sQuery(id+"F0.wireOp",EDGE,"E12.left"),sQuery(id+"F0.wireOp",EDGE,"E13.0.1.1"),sQuery(id+"F0.wireOp",EDGE,"E13.0.1.2"),sQuery(id+"F0.wireOp",EDGE,"E13.0.1.3"),sQuery(id+"F0.wireOp",EDGE,"E13.0.2.1"),sQuery(id+"F0.wireOp",EDGE,"E13.0.2.3"),sQuery(id+"F0.wireOp",EDGE,"E17.trimOffspring"),sQuery(id+"F0.wireOp",EDGE,"E20.5.0.0"),sQuery(id+"F0.wireOp",EDGE,"E20.5.0.1"),sQuery(id+"F0.wireOp",EDGE,"E20.5.0.2"),sQuery(id+"F0.wireOp",EDGE,"E20.6.0.0"),sQuery(id+"F0.wireOp",EDGE,"E20.6.0.1"),sQuery(id+"F0.wireOp",EDGE,"E20.6.0.2"),sQuery(id+"F0.wireOp",EDGE,"E20.7.0.0"),sQuery(id+"F0.wireOp",EDGE,"E20.7.0.1"),sQuery(id+"F0.wireOp",EDGE,"E20.7.0.2"),sQuery(id+"F0.wireOp",EDGE,"E20.8.0.0"),sQuery(id+"F0.wireOp",EDGE,"E20.8.0.1"),sQuery(id+"F0.wireOp",EDGE,"E20.8.0.2"),sQuery(id+"F0.wireOp",EDGE,"E20.9.0.0"),sQuery(id+"F0.wireOp",EDGE,"E20.9.0.2"),sQuery(id+"F0.wireOp",EDGE,"E24.trimOffspring"),sQuery(id+"F0.wireOp",EDGE,"E25.trimOffspring"),sQuery(id+"F0.wireOp",EDGE,"E26.trimOffspring"),sQuery(id+"F0.wireOp",EDGE,"E27.trimOffspring"),sQuery(id+"F0.wireOp",EDGE,"E28.trimOffspring")])]});
            var Q1;
            Q1=makeQuery(id+"F5.opPattern","COPY",BODY,{"derivedFrom":makeQuery(id+"F2.opExtrude","SWEPT_BODY",BODY,{"disambiguationData":[OSD([sQuery(id+"F0.wireOp",EDGE,"E0.right"),sQuery(id+"F0.wireOp",EDGE,"E1"),sQuery(id+"F0.wireOp",EDGE,"E2"),sQuery(id+"F0.wireOp",EDGE,"E12.top"),sQuery(id+"F0.wireOp",EDGE,"E12.left"),sQuery(id+"F0.wireOp",EDGE,"E13.0.1.1"),sQuery(id+"F0.wireOp",EDGE,"E13.0.1.2"),sQuery(id+"F0.wireOp",EDGE,"E13.0.1.3"),sQuery(id+"F0.wireOp",EDGE,"E13.0.2.1"),sQuery(id+"F0.wireOp",EDGE,"E13.0.2.3"),sQuery(id+"F0.wireOp",EDGE,"E17.trimOffspring"),sQuery(id+"F0.wireOp",EDGE,"E20.5.0.0"),sQuery(id+"F0.wireOp",EDGE,"E20.5.0.1"),sQuery(id+"F0.wireOp",EDGE,"E20.5.0.2"),sQuery(id+"F0.wireOp",EDGE,"E20.6.0.0"),sQuery(id+"F0.wireOp",EDGE,"E20.6.0.1"),sQuery(id+"F0.wireOp",EDGE,"E20.6.0.2"),sQuery(id+"F0.wireOp",EDGE,"E20.7.0.0"),sQuery(id+"F0.wireOp",EDGE,"E20.7.0.1"),sQuery(id+"F0.wireOp",EDGE,"E20.7.0.2"),sQuery(id+"F0.wireOp",EDGE,"E20.8.0.0"),sQuery(id+"F0.wireOp",EDGE,"E20.8.0.1"),sQuery(id+"F0.wireOp",EDGE,"E20.8.0.2"),sQuery(id+"F0.wireOp",EDGE,"E20.9.0.0"),sQuery(id+"F0.wireOp",EDGE,"E20.9.0.2"),sQuery(id+"F0.wireOp",EDGE,"E24.trimOffspring"),sQuery(id+"F0.wireOp",EDGE,"E25.trimOffspring"),sQuery(id+"F0.wireOp",EDGE,"E26.trimOffspring"),sQuery(id+"F0.wireOp",EDGE,"E27.trimOffspring"),sQuery(id+"F0.wireOp",EDGE,"E28.trimOffspring")])]}),"instanceName":"1"});
            var Q2;
            Q2=makeQuery(id+"F9.opExtrude","SWEPT_BODY",BODY,{"disambiguationData":[OSD([sQuery(id+"F3.wireOp",EDGE,"E29.bottom"),sQuery(id+"F3.wireOp",EDGE,"E29.left"),sQuery(id+"F3.wireOp",EDGE,"E29.right"),sQuery(id+"F3.wireOp",EDGE,"E30.top"),sQuery(id+"F3.wireOp",EDGE,"E30.right"),sQuery(id+"F3.wireOp",EDGE,"E32.1.0.0"),sQuery(id+"F3.wireOp",EDGE,"E32.1.0.1"),sQuery(id+"F3.wireOp",EDGE,"E32.1.0.2"),sQuery(id+"F3.wireOp",EDGE,"E32.2.0.0"),sQuery(id+"F3.wireOp",EDGE,"E32.2.0.1"),sQuery(id+"F3.wireOp",EDGE,"E32.2.0.2"),sQuery(id+"F3.wireOp",EDGE,"E32.3.0.0"),sQuery(id+"F3.wireOp",EDGE,"E32.3.0.1"),sQuery(id+"F3.wireOp",EDGE,"E32.3.0.2"),sQuery(id+"F3.wireOp",EDGE,"E32.4.0.0"),sQuery(id+"F3.wireOp",EDGE,"E32.4.0.1"),sQuery(id+"F3.wireOp",EDGE,"E32.4.0.2"),sQuery(id+"F3.wireOp",EDGE,"E34.trimOffspring"),sQuery(id+"F3.wireOp",EDGE,"E35.trimOffspring"),sQuery(id+"F3.wireOp",EDGE,"E36.trimOffspring"),sQuery(id+"F3.wireOp",EDGE,"E37.trimOffspring"),sQuery(id+"F3.wireOp",EDGE,"E42")])]});
            booleanBodies(context, id + "F10", {"operationType" : BooleanOperationType.SUBTRACTION, "tools" : qUnion([Q0, Q1]), "targets" : qUnion([Q2]), "keepTools" : true});
        }
        {
            var Q0;
            Q0=makeQuery(id+"F1.opExtrude","SWEPT_BODY",BODY,{"disambiguationData":[OSD([sQuery(id+"F0.wireOp",EDGE,"E0.bottom"),sQuery(id+"F0.wireOp",EDGE,"E0.top"),sQuery(id+"F0.wireOp",EDGE,"E0.left"),sQuery(id+"F0.wireOp",EDGE,"E1"),sQuery(id+"F0.wireOp",EDGE,"E2"),sQuery(id+"F0.wireOp",EDGE,"E3.bottom"),sQuery(id+"F0.wireOp",EDGE,"E3.top"),sQuery(id+"F0.wireOp",EDGE,"E3.right"),sQuery(id+"F0.wireOp",EDGE,"E4.trimOffspring"),sQuery(id+"F0.wireOp",EDGE,"E5.0.1.0"),sQuery(id+"F0.wireOp",EDGE,"E5.0.1.1"),sQuery(id+"F0.wireOp",EDGE,"E5.0.1.2"),sQuery(id+"F0.wireOp",EDGE,"E5.0.2.0"),sQuery(id+"F0.wireOp",EDGE,"E5.0.2.1"),sQuery(id+"F0.wireOp",EDGE,"E5.0.2.2"),sQuery(id+"F0.wireOp",EDGE,"E5.0.3.0"),sQuery(id+"F0.wireOp",EDGE,"E5.0.3.1"),sQuery(id+"F0.wireOp",EDGE,"E5.0.3.2"),sQuery(id+"F0.wireOp",EDGE,"E5.0.4.0"),sQuery(id+"F0.wireOp",EDGE,"E5.0.4.1"),sQuery(id+"F0.wireOp",EDGE,"E6.trimOffspring"),sQuery(id+"F0.wireOp",EDGE,"E7.trimOffspring"),sQuery(id+"F0.wireOp",EDGE,"E8.trimOffspring"),sQuery(id+"F0.wireOp",EDGE,"E9.top"),sQuery(id+"F0.wireOp",EDGE,"E9.left"),sQuery(id+"F0.wireOp",EDGE,"E9.right"),sQuery(id+"F0.wireOp",EDGE,"E11.1.0.0"),sQuery(id+"F0.wireOp",EDGE,"E11.1.0.1"),sQuery(id+"F0.wireOp",EDGE,"E10.trimOffspring"),sQuery(id+"F0.wireOp",EDGE,"E11.1.0.3"),sQuery(id+"F0.wireOp",EDGE,"E11.2.0.0"),sQuery(id+"F0.wireOp",EDGE,"E11.2.0.1"),sQuery(id+"F0.wireOp",EDGE,"E11.2.0.3"),sQuery(id+"F0.wireOp",EDGE,"E11.3.0.0"),sQuery(id+"F0.wireOp",EDGE,"E11.3.0.1"),sQuery(id+"F0.wireOp",EDGE,"E11.3.0.3"),sQuery(id+"F0.wireOp",EDGE,"E11.4.0.0"),sQuery(id+"F0.wireOp",EDGE,"E11.4.0.1"),sQuery(id+"F0.wireOp",EDGE,"E11.4.0.3"),sQuery(id+"F0.wireOp",EDGE,"E11.5.0.0"),sQuery(id+"F0.wireOp",EDGE,"E11.5.0.1"),sQuery(id+"F0.wireOp",EDGE,"E11.5.0.3"),sQuery(id+"F0.wireOp",EDGE,"E11.6.0.0"),sQuery(id+"F0.wireOp",EDGE,"E11.6.0.1"),sQuery(id+"F0.wireOp",EDGE,"E11.6.0.3"),sQuery(id+"F0.wireOp",EDGE,"E11.7.0.0"),sQuery(id+"F0.wireOp",EDGE,"E11.7.0.1"),sQuery(id+"F0.wireOp",EDGE,"E11.7.0.3"),sQuery(id+"F0.wireOp",EDGE,"E11.8.0.0"),sQuery(id+"F0.wireOp",EDGE,"E11.8.0.1"),sQuery(id+"F0.wireOp",EDGE,"E11.8.0.3"),sQuery(id+"F0.wireOp",EDGE,"E11.9.0.0"),sQuery(id+"F0.wireOp",EDGE,"E11.9.0.3"),sQuery(id+"F0.wireOp",EDGE,"E11.2.0.2"),sQuery(id+"F0.wireOp",EDGE,"E11.3.0.2"),sQuery(id+"F0.wireOp",EDGE,"E11.4.0.2"),sQuery(id+"F0.wireOp",EDGE,"E11.5.0.2"),sQuery(id+"F0.wireOp",EDGE,"E11.6.0.2"),sQuery(id+"F0.wireOp",EDGE,"E11.7.0.2"),sQuery(id+"F0.wireOp",EDGE,"E11.8.0.2"),sQuery(id+"F0.wireOp",EDGE,"E11.9.0.2"),sQuery(id+"F0.wireOp",EDGE,"E13.0.2.2"),sQuery(id+"F0.wireOp",EDGE,"E13.0.3.1"),sQuery(id+"F0.wireOp",EDGE,"E13.0.3.2"),sQuery(id+"F0.wireOp",EDGE,"E13.0.3.3"),sQuery(id+"F0.wireOp",EDGE,"E13.0.4.1"),sQuery(id+"F0.wireOp",EDGE,"E13.0.4.2"),sQuery(id+"F0.wireOp",EDGE,"E13.0.4.3"),sQuery(id+"F0.wireOp",EDGE,"E14.trimOffspring"),sQuery(id+"F0.wireOp",EDGE,"E15.trimOffspring"),sQuery(id+"F0.wireOp",EDGE,"E16.trimOffspring"),sQuery(id+"F0.wireOp",EDGE,"E18.top"),sQuery(id+"F0.wireOp",EDGE,"E18.left"),sQuery(id+"F0.wireOp",EDGE,"E18.right"),sQuery(id+"F0.wireOp",EDGE,"E19.trimOffspring"),sQuery(id+"F0.wireOp",EDGE,"E20.1.0.0"),sQuery(id+"F0.wireOp",EDGE,"E20.1.0.1"),sQuery(id+"F0.wireOp",EDGE,"E20.1.0.2"),sQuery(id+"F0.wireOp",EDGE,"E20.2.0.0"),sQuery(id+"F0.wireOp",EDGE,"E20.2.0.1"),sQuery(id+"F0.wireOp",EDGE,"E20.2.0.2"),sQuery(id+"F0.wireOp",EDGE,"E20.3.0.0"),sQuery(id+"F0.wireOp",EDGE,"E20.3.0.1"),sQuery(id+"F0.wireOp",EDGE,"E20.3.0.2"),sQuery(id+"F0.wireOp",EDGE,"E20.4.0.0"),sQuery(id+"F0.wireOp",EDGE,"E20.4.0.1"),sQuery(id+"F0.wireOp",EDGE,"E20.4.0.2"),sQuery(id+"F0.wireOp",EDGE,"E21.trimOffspring"),sQuery(id+"F0.wireOp",EDGE,"E22.trimOffspring"),sQuery(id+"F0.wireOp",EDGE,"E23.trimOffspring")])]});
            var Q1;
            Q1=makeQuery(id+"F4.opPattern","COPY",BODY,{"derivedFrom":makeQuery(id+"F1.opExtrude","SWEPT_BODY",BODY,{"disambiguationData":[OSD([sQuery(id+"F0.wireOp",EDGE,"E0.bottom"),sQuery(id+"F0.wireOp",EDGE,"E0.top"),sQuery(id+"F0.wireOp",EDGE,"E0.left"),sQuery(id+"F0.wireOp",EDGE,"E1"),sQuery(id+"F0.wireOp",EDGE,"E2"),sQuery(id+"F0.wireOp",EDGE,"E3.bottom"),sQuery(id+"F0.wireOp",EDGE,"E3.top"),sQuery(id+"F0.wireOp",EDGE,"E3.right"),sQuery(id+"F0.wireOp",EDGE,"E4.trimOffspring"),sQuery(id+"F0.wireOp",EDGE,"E5.0.1.0"),sQuery(id+"F0.wireOp",EDGE,"E5.0.1.1"),sQuery(id+"F0.wireOp",EDGE,"E5.0.1.2"),sQuery(id+"F0.wireOp",EDGE,"E5.0.2.0"),sQuery(id+"F0.wireOp",EDGE,"E5.0.2.1"),sQuery(id+"F0.wireOp",EDGE,"E5.0.2.2"),sQuery(id+"F0.wireOp",EDGE,"E5.0.3.0"),sQuery(id+"F0.wireOp",EDGE,"E5.0.3.1"),sQuery(id+"F0.wireOp",EDGE,"E5.0.3.2"),sQuery(id+"F0.wireOp",EDGE,"E5.0.4.0"),sQuery(id+"F0.wireOp",EDGE,"E5.0.4.1"),sQuery(id+"F0.wireOp",EDGE,"E6.trimOffspring"),sQuery(id+"F0.wireOp",EDGE,"E7.trimOffspring"),sQuery(id+"F0.wireOp",EDGE,"E8.trimOffspring"),sQuery(id+"F0.wireOp",EDGE,"E9.top"),sQuery(id+"F0.wireOp",EDGE,"E9.left"),sQuery(id+"F0.wireOp",EDGE,"E9.right"),sQuery(id+"F0.wireOp",EDGE,"E11.1.0.0"),sQuery(id+"F0.wireOp",EDGE,"E11.1.0.1"),sQuery(id+"F0.wireOp",EDGE,"E10.trimOffspring"),sQuery(id+"F0.wireOp",EDGE,"E11.1.0.3"),sQuery(id+"F0.wireOp",EDGE,"E11.2.0.0"),sQuery(id+"F0.wireOp",EDGE,"E11.2.0.1"),sQuery(id+"F0.wireOp",EDGE,"E11.2.0.3"),sQuery(id+"F0.wireOp",EDGE,"E11.3.0.0"),sQuery(id+"F0.wireOp",EDGE,"E11.3.0.1"),sQuery(id+"F0.wireOp",EDGE,"E11.3.0.3"),sQuery(id+"F0.wireOp",EDGE,"E11.4.0.0"),sQuery(id+"F0.wireOp",EDGE,"E11.4.0.1"),sQuery(id+"F0.wireOp",EDGE,"E11.4.0.3"),sQuery(id+"F0.wireOp",EDGE,"E11.5.0.0"),sQuery(id+"F0.wireOp",EDGE,"E11.5.0.1"),sQuery(id+"F0.wireOp",EDGE,"E11.5.0.3"),sQuery(id+"F0.wireOp",EDGE,"E11.6.0.0"),sQuery(id+"F0.wireOp",EDGE,"E11.6.0.1"),sQuery(id+"F0.wireOp",EDGE,"E11.6.0.3"),sQuery(id+"F0.wireOp",EDGE,"E11.7.0.0"),sQuery(id+"F0.wireOp",EDGE,"E11.7.0.1"),sQuery(id+"F0.wireOp",EDGE,"E11.7.0.3"),sQuery(id+"F0.wireOp",EDGE,"E11.8.0.0"),sQuery(id+"F0.wireOp",EDGE,"E11.8.0.1"),sQuery(id+"F0.wireOp",EDGE,"E11.8.0.3"),sQuery(id+"F0.wireOp",EDGE,"E11.9.0.0"),sQuery(id+"F0.wireOp",EDGE,"E11.9.0.3"),sQuery(id+"F0.wireOp",EDGE,"E11.2.0.2"),sQuery(id+"F0.wireOp",EDGE,"E11.3.0.2"),sQuery(id+"F0.wireOp",EDGE,"E11.4.0.2"),sQuery(id+"F0.wireOp",EDGE,"E11.5.0.2"),sQuery(id+"F0.wireOp",EDGE,"E11.6.0.2"),sQuery(id+"F0.wireOp",EDGE,"E11.7.0.2"),sQuery(id+"F0.wireOp",EDGE,"E11.8.0.2"),sQuery(id+"F0.wireOp",EDGE,"E11.9.0.2"),sQuery(id+"F0.wireOp",EDGE,"E13.0.2.2"),sQuery(id+"F0.wireOp",EDGE,"E13.0.3.1"),sQuery(id+"F0.wireOp",EDGE,"E13.0.3.2"),sQuery(id+"F0.wireOp",EDGE,"E13.0.3.3"),sQuery(id+"F0.wireOp",EDGE,"E13.0.4.1"),sQuery(id+"F0.wireOp",EDGE,"E13.0.4.2"),sQuery(id+"F0.wireOp",EDGE,"E13.0.4.3"),sQuery(id+"F0.wireOp",EDGE,"E14.trimOffspring"),sQuery(id+"F0.wireOp",EDGE,"E15.trimOffspring"),sQuery(id+"F0.wireOp",EDGE,"E16.trimOffspring"),sQuery(id+"F0.wireOp",EDGE,"E18.top"),sQuery(id+"F0.wireOp",EDGE,"E18.left"),sQuery(id+"F0.wireOp",EDGE,"E18.right"),sQuery(id+"F0.wireOp",EDGE,"E19.trimOffspring"),sQuery(id+"F0.wireOp",EDGE,"E20.1.0.0"),sQuery(id+"F0.wireOp",EDGE,"E20.1.0.1"),sQuery(id+"F0.wireOp",EDGE,"E20.1.0.2"),sQuery(id+"F0.wireOp",EDGE,"E20.2.0.0"),sQuery(id+"F0.wireOp",EDGE,"E20.2.0.1"),sQuery(id+"F0.wireOp",EDGE,"E20.2.0.2"),sQuery(id+"F0.wireOp",EDGE,"E20.3.0.0"),sQuery(id+"F0.wireOp",EDGE,"E20.3.0.1"),sQuery(id+"F0.wireOp",EDGE,"E20.3.0.2"),sQuery(id+"F0.wireOp",EDGE,"E20.4.0.0"),sQuery(id+"F0.wireOp",EDGE,"E20.4.0.1"),sQuery(id+"F0.wireOp",EDGE,"E20.4.0.2"),sQuery(id+"F0.wireOp",EDGE,"E21.trimOffspring"),sQuery(id+"F0.wireOp",EDGE,"E22.trimOffspring"),sQuery(id+"F0.wireOp",EDGE,"E23.trimOffspring")])]}),"instanceName":"1"});
            var Q2;
            Q2=makeQuery(id+"F8.opExtrude","SWEPT_BODY",BODY,{"disambiguationData":[OSD([sQuery(id+"F3.wireOp",EDGE,"E29.top"),sQuery(id+"F3.wireOp",EDGE,"E29.left"),sQuery(id+"F3.wireOp",EDGE,"E29.right"),sQuery(id+"F3.wireOp",EDGE,"E31.top"),sQuery(id+"F3.wireOp",EDGE,"E31.right"),sQuery(id+"F3.wireOp",EDGE,"E33.1.0.1"),sQuery(id+"F3.wireOp",EDGE,"E33.1.0.2"),sQuery(id+"F3.wireOp",EDGE,"E33.1.0.3"),sQuery(id+"F3.wireOp",EDGE,"E33.2.0.1"),sQuery(id+"F3.wireOp",EDGE,"E33.2.0.2"),sQuery(id+"F3.wireOp",EDGE,"E33.2.0.3"),sQuery(id+"F3.wireOp",EDGE,"E33.3.0.1"),sQuery(id+"F3.wireOp",EDGE,"E33.3.0.2"),sQuery(id+"F3.wireOp",EDGE,"E33.3.0.3"),sQuery(id+"F3.wireOp",EDGE,"E33.4.0.1"),sQuery(id+"F3.wireOp",EDGE,"E33.4.0.2"),sQuery(id+"F3.wireOp",EDGE,"E33.4.0.3"),sQuery(id+"F3.wireOp",EDGE,"E38.trimOffspring"),sQuery(id+"F3.wireOp",EDGE,"E39.trimOffspring"),sQuery(id+"F3.wireOp",EDGE,"E40.trimOffspring"),sQuery(id+"F3.wireOp",EDGE,"E41.trimOffspring"),sQuery(id+"F3.wireOp",EDGE,"E42")])]});
            booleanBodies(context, id + "F11", {"operationType" : BooleanOperationType.SUBTRACTION, "tools" : qUnion([Q0, Q1]), "targets" : qUnion([Q2]), "keepTools" : true});
        }
        {
            var Q0;
            Q0=qCreatedBy(makeId("Top.planeOp"),FACE);
            var sketch = newSketch(context, id + "F12", { "sketchPlane" : qUnion([Q0])});
            skLineSegment(sketch, "E43.bottom", {"start": v(-97, 200) * mm, "end": v(3, 200) * mm});
            skLineSegment(sketch, "E43.top", {"start": v(-97, 0) * mm, "end": v(3, 0) * mm});
            skLineSegment(sketch, "E43.left", {"start": v(-97, 200) * mm, "end": v(-97, 0) * mm});
            skLineSegment(sketch, "E43.right", {"start": v(3, 200) * mm, "end": v(3, 0) * mm});
            skLineSegment(sketch, "E44", {"start": v(-97, 100) * mm, "end": v(3, 100) * mm});
            skSolve(sketch);
        }
        {
            var Q0;
            {var subQ0=sQuery(id+"F12.wireOp",EDGE,"E43.top");Q0=makeQuery(id+"F12.imprint","IMPRINT",FACE,{"disambiguationData":[TD([[makeQuery(id+"F12.imprint","IMPRINT",EDGE,{"derivedFrom":subQ0}),1.0]])]});}
            extrude(context, id + "F13", {"entities" : qUnion([Q0]), "depth" : -3 * mm, "offsetDistance" : 25 * mm});
        }
        {
            var Q0;
            {var subQ0=sQuery(id+"F12.wireOp",EDGE,"E43.bottom");Q0=makeQuery(id+"F12.imprint","IMPRINT",FACE,{"disambiguationData":[TD([[makeQuery(id+"F12.imprint","IMPRINT",EDGE,{"derivedFrom":subQ0}),-1.0]])]});}
            extrude(context, id + "F14", {"entities" : qUnion([Q0]), "depth" : -3 * mm, "offsetDistance" : 25 * mm});
        }
        {
            var Q0;
            Q0 = qSketchRegion(id + "F12", true);
            extrude(context, id + "F15", {"entities" : qUnion([Q0]), "oppositeDirection" : true, "depth" : 100 * mm, "offsetDistance" : 25 * mm, "hasSecondDirection" : true, "secondDirectionOppositeDirection" : true, "secondDirectionDepth" : 97 * mm});
        }
        {
            var Q0;
            Q0=makeQuery(id+"F6.opExtrude","SWEPT_BODY",BODY,{"disambiguationData":[OSD([sQuery(id+"F3.wireOp",EDGE,"E29.bottom"),sQuery(id+"F3.wireOp",EDGE,"E29.top"),sQuery(id+"F3.wireOp",EDGE,"E29.left"),sQuery(id+"F3.wireOp",EDGE,"E29.right"),sQuery(id+"F3.wireOp",EDGE,"E30.top"),sQuery(id+"F3.wireOp",EDGE,"E30.right"),sQuery(id+"F3.wireOp",EDGE,"E31.top"),sQuery(id+"F3.wireOp",EDGE,"E31.right"),sQuery(id+"F3.wireOp",EDGE,"E32.1.0.0"),sQuery(id+"F3.wireOp",EDGE,"E32.1.0.1"),sQuery(id+"F3.wireOp",EDGE,"E32.1.0.2"),sQuery(id+"F3.wireOp",EDGE,"E32.2.0.0"),sQuery(id+"F3.wireOp",EDGE,"E32.2.0.1"),sQuery(id+"F3.wireOp",EDGE,"E32.2.0.2"),sQuery(id+"F3.wireOp",EDGE,"E32.3.0.0"),sQuery(id+"F3.wireOp",EDGE,"E32.3.0.1"),sQuery(id+"F3.wireOp",EDGE,"E32.3.0.2"),sQuery(id+"F3.wireOp",EDGE,"E32.4.0.0"),sQuery(id+"F3.wireOp",EDGE,"E32.4.0.1"),sQuery(id+"F3.wireOp",EDGE,"E32.4.0.2"),sQuery(id+"F3.wireOp",EDGE,"E33.1.0.1"),sQuery(id+"F3.wireOp",EDGE,"E33.1.0.2"),sQuery(id+"F3.wireOp",EDGE,"E33.1.0.3"),sQuery(id+"F3.wireOp",EDGE,"E33.2.0.1"),sQuery(id+"F3.wireOp",EDGE,"E33.2.0.2"),sQuery(id+"F3.wireOp",EDGE,"E33.2.0.3"),sQuery(id+"F3.wireOp",EDGE,"E33.3.0.1"),sQuery(id+"F3.wireOp",EDGE,"E33.3.0.2"),sQuery(id+"F3.wireOp",EDGE,"E33.3.0.3"),sQuery(id+"F3.wireOp",EDGE,"E33.4.0.1"),sQuery(id+"F3.wireOp",EDGE,"E33.4.0.2"),sQuery(id+"F3.wireOp",EDGE,"E33.4.0.3"),sQuery(id+"F3.wireOp",EDGE,"E34.trimOffspring"),sQuery(id+"F3.wireOp",EDGE,"E35.trimOffspring"),sQuery(id+"F3.wireOp",EDGE,"E36.trimOffspring"),sQuery(id+"F3.wireOp",EDGE,"E37.trimOffspring"),sQuery(id+"F3.wireOp",EDGE,"E38.trimOffspring"),sQuery(id+"F3.wireOp",EDGE,"E39.trimOffspring"),sQuery(id+"F3.wireOp",EDGE,"E40.trimOffspring"),sQuery(id+"F3.wireOp",EDGE,"E41.trimOffspring")])]});
            var Q1;
            Q1=makeQuery(id+"F1.opExtrude","SWEPT_BODY",BODY,{"disambiguationData":[OSD([sQuery(id+"F0.wireOp",EDGE,"E0.bottom"),sQuery(id+"F0.wireOp",EDGE,"E0.top"),sQuery(id+"F0.wireOp",EDGE,"E0.left"),sQuery(id+"F0.wireOp",EDGE,"E1"),sQuery(id+"F0.wireOp",EDGE,"E2"),sQuery(id+"F0.wireOp",EDGE,"E3.bottom"),sQuery(id+"F0.wireOp",EDGE,"E3.top"),sQuery(id+"F0.wireOp",EDGE,"E3.right"),sQuery(id+"F0.wireOp",EDGE,"E4.trimOffspring"),sQuery(id+"F0.wireOp",EDGE,"E5.0.1.0"),sQuery(id+"F0.wireOp",EDGE,"E5.0.1.1"),sQuery(id+"F0.wireOp",EDGE,"E5.0.1.2"),sQuery(id+"F0.wireOp",EDGE,"E5.0.2.0"),sQuery(id+"F0.wireOp",EDGE,"E5.0.2.1"),sQuery(id+"F0.wireOp",EDGE,"E5.0.2.2"),sQuery(id+"F0.wireOp",EDGE,"E5.0.3.0"),sQuery(id+"F0.wireOp",EDGE,"E5.0.3.1"),sQuery(id+"F0.wireOp",EDGE,"E5.0.3.2"),sQuery(id+"F0.wireOp",EDGE,"E5.0.4.0"),sQuery(id+"F0.wireOp",EDGE,"E5.0.4.1"),sQuery(id+"F0.wireOp",EDGE,"E6.trimOffspring"),sQuery(id+"F0.wireOp",EDGE,"E7.trimOffspring"),sQuery(id+"F0.wireOp",EDGE,"E8.trimOffspring"),sQuery(id+"F0.wireOp",EDGE,"E9.top"),sQuery(id+"F0.wireOp",EDGE,"E9.left"),sQuery(id+"F0.wireOp",EDGE,"E9.right"),sQuery(id+"F0.wireOp",EDGE,"E11.1.0.0"),sQuery(id+"F0.wireOp",EDGE,"E11.1.0.1"),sQuery(id+"F0.wireOp",EDGE,"E10.trimOffspring"),sQuery(id+"F0.wireOp",EDGE,"E11.1.0.3"),sQuery(id+"F0.wireOp",EDGE,"E11.2.0.0"),sQuery(id+"F0.wireOp",EDGE,"E11.2.0.1"),sQuery(id+"F0.wireOp",EDGE,"E11.2.0.3"),sQuery(id+"F0.wireOp",EDGE,"E11.3.0.0"),sQuery(id+"F0.wireOp",EDGE,"E11.3.0.1"),sQuery(id+"F0.wireOp",EDGE,"E11.3.0.3"),sQuery(id+"F0.wireOp",EDGE,"E11.4.0.0"),sQuery(id+"F0.wireOp",EDGE,"E11.4.0.1"),sQuery(id+"F0.wireOp",EDGE,"E11.4.0.3"),sQuery(id+"F0.wireOp",EDGE,"E11.5.0.0"),sQuery(id+"F0.wireOp",EDGE,"E11.5.0.1"),sQuery(id+"F0.wireOp",EDGE,"E11.5.0.3"),sQuery(id+"F0.wireOp",EDGE,"E11.6.0.0"),sQuery(id+"F0.wireOp",EDGE,"E11.6.0.1"),sQuery(id+"F0.wireOp",EDGE,"E11.6.0.3"),sQuery(id+"F0.wireOp",EDGE,"E11.7.0.0"),sQuery(id+"F0.wireOp",EDGE,"E11.7.0.1"),sQuery(id+"F0.wireOp",EDGE,"E11.7.0.3"),sQuery(id+"F0.wireOp",EDGE,"E11.8.0.0"),sQuery(id+"F0.wireOp",EDGE,"E11.8.0.1"),sQuery(id+"F0.wireOp",EDGE,"E11.8.0.3"),sQuery(id+"F0.wireOp",EDGE,"E11.9.0.0"),sQuery(id+"F0.wireOp",EDGE,"E11.9.0.3"),sQuery(id+"F0.wireOp",EDGE,"E11.2.0.2"),sQuery(id+"F0.wireOp",EDGE,"E11.3.0.2"),sQuery(id+"F0.wireOp",EDGE,"E11.4.0.2"),sQuery(id+"F0.wireOp",EDGE,"E11.5.0.2"),sQuery(id+"F0.wireOp",EDGE,"E11.6.0.2"),sQuery(id+"F0.wireOp",EDGE,"E11.7.0.2"),sQuery(id+"F0.wireOp",EDGE,"E11.8.0.2"),sQuery(id+"F0.wireOp",EDGE,"E11.9.0.2"),sQuery(id+"F0.wireOp",EDGE,"E13.0.2.2"),sQuery(id+"F0.wireOp",EDGE,"E13.0.3.1"),sQuery(id+"F0.wireOp",EDGE,"E13.0.3.2"),sQuery(id+"F0.wireOp",EDGE,"E13.0.3.3"),sQuery(id+"F0.wireOp",EDGE,"E13.0.4.1"),sQuery(id+"F0.wireOp",EDGE,"E13.0.4.2"),sQuery(id+"F0.wireOp",EDGE,"E13.0.4.3"),sQuery(id+"F0.wireOp",EDGE,"E14.trimOffspring"),sQuery(id+"F0.wireOp",EDGE,"E15.trimOffspring"),sQuery(id+"F0.wireOp",EDGE,"E16.trimOffspring"),sQuery(id+"F0.wireOp",EDGE,"E18.top"),sQuery(id+"F0.wireOp",EDGE,"E18.left"),sQuery(id+"F0.wireOp",EDGE,"E18.right"),sQuery(id+"F0.wireOp",EDGE,"E19.trimOffspring"),sQuery(id+"F0.wireOp",EDGE,"E20.1.0.0"),sQuery(id+"F0.wireOp",EDGE,"E20.1.0.1"),sQuery(id+"F0.wireOp",EDGE,"E20.1.0.2"),sQuery(id+"F0.wireOp",EDGE,"E20.2.0.0"),sQuery(id+"F0.wireOp",EDGE,"E20.2.0.1"),sQuery(id+"F0.wireOp",EDGE,"E20.2.0.2"),sQuery(id+"F0.wireOp",EDGE,"E20.3.0.0"),sQuery(id+"F0.wireOp",EDGE,"E20.3.0.1"),sQuery(id+"F0.wireOp",EDGE,"E20.3.0.2"),sQuery(id+"F0.wireOp",EDGE,"E20.4.0.0"),sQuery(id+"F0.wireOp",EDGE,"E20.4.0.1"),sQuery(id+"F0.wireOp",EDGE,"E20.4.0.2"),sQuery(id+"F0.wireOp",EDGE,"E21.trimOffspring"),sQuery(id+"F0.wireOp",EDGE,"E22.trimOffspring"),sQuery(id+"F0.wireOp",EDGE,"E23.trimOffspring")])]});
            var Q2;
            Q2=makeQuery(id+"F8.opExtrude","SWEPT_BODY",BODY,{"disambiguationData":[OSD([sQuery(id+"F3.wireOp",EDGE,"E29.top"),sQuery(id+"F3.wireOp",EDGE,"E29.left"),sQuery(id+"F3.wireOp",EDGE,"E29.right"),sQuery(id+"F3.wireOp",EDGE,"E31.top"),sQuery(id+"F3.wireOp",EDGE,"E31.right"),sQuery(id+"F3.wireOp",EDGE,"E33.1.0.1"),sQuery(id+"F3.wireOp",EDGE,"E33.1.0.2"),sQuery(id+"F3.wireOp",EDGE,"E33.1.0.3"),sQuery(id+"F3.wireOp",EDGE,"E33.2.0.1"),sQuery(id+"F3.wireOp",EDGE,"E33.2.0.2"),sQuery(id+"F3.wireOp",EDGE,"E33.2.0.3"),sQuery(id+"F3.wireOp",EDGE,"E33.3.0.1"),sQuery(id+"F3.wireOp",EDGE,"E33.3.0.2"),sQuery(id+"F3.wireOp",EDGE,"E33.3.0.3"),sQuery(id+"F3.wireOp",EDGE,"E33.4.0.1"),sQuery(id+"F3.wireOp",EDGE,"E33.4.0.2"),sQuery(id+"F3.wireOp",EDGE,"E33.4.0.3"),sQuery(id+"F3.wireOp",EDGE,"E38.trimOffspring"),sQuery(id+"F3.wireOp",EDGE,"E39.trimOffspring"),sQuery(id+"F3.wireOp",EDGE,"E40.trimOffspring"),sQuery(id+"F3.wireOp",EDGE,"E41.trimOffspring"),sQuery(id+"F3.wireOp",EDGE,"E42")])]});
            var Q3;
            Q3=makeQuery(id+"F4.opPattern","COPY",BODY,{"derivedFrom":makeQuery(id+"F1.opExtrude","SWEPT_BODY",BODY,{"disambiguationData":[OSD([sQuery(id+"F0.wireOp",EDGE,"E0.bottom"),sQuery(id+"F0.wireOp",EDGE,"E0.top"),sQuery(id+"F0.wireOp",EDGE,"E0.left"),sQuery(id+"F0.wireOp",EDGE,"E1"),sQuery(id+"F0.wireOp",EDGE,"E2"),sQuery(id+"F0.wireOp",EDGE,"E3.bottom"),sQuery(id+"F0.wireOp",EDGE,"E3.top"),sQuery(id+"F0.wireOp",EDGE,"E3.right"),sQuery(id+"F0.wireOp",EDGE,"E4.trimOffspring"),sQuery(id+"F0.wireOp",EDGE,"E5.0.1.0"),sQuery(id+"F0.wireOp",EDGE,"E5.0.1.1"),sQuery(id+"F0.wireOp",EDGE,"E5.0.1.2"),sQuery(id+"F0.wireOp",EDGE,"E5.0.2.0"),sQuery(id+"F0.wireOp",EDGE,"E5.0.2.1"),sQuery(id+"F0.wireOp",EDGE,"E5.0.2.2"),sQuery(id+"F0.wireOp",EDGE,"E5.0.3.0"),sQuery(id+"F0.wireOp",EDGE,"E5.0.3.1"),sQuery(id+"F0.wireOp",EDGE,"E5.0.3.2"),sQuery(id+"F0.wireOp",EDGE,"E5.0.4.0"),sQuery(id+"F0.wireOp",EDGE,"E5.0.4.1"),sQuery(id+"F0.wireOp",EDGE,"E6.trimOffspring"),sQuery(id+"F0.wireOp",EDGE,"E7.trimOffspring"),sQuery(id+"F0.wireOp",EDGE,"E8.trimOffspring"),sQuery(id+"F0.wireOp",EDGE,"E9.top"),sQuery(id+"F0.wireOp",EDGE,"E9.left"),sQuery(id+"F0.wireOp",EDGE,"E9.right"),sQuery(id+"F0.wireOp",EDGE,"E11.1.0.0"),sQuery(id+"F0.wireOp",EDGE,"E11.1.0.1"),sQuery(id+"F0.wireOp",EDGE,"E10.trimOffspring"),sQuery(id+"F0.wireOp",EDGE,"E11.1.0.3"),sQuery(id+"F0.wireOp",EDGE,"E11.2.0.0"),sQuery(id+"F0.wireOp",EDGE,"E11.2.0.1"),sQuery(id+"F0.wireOp",EDGE,"E11.2.0.3"),sQuery(id+"F0.wireOp",EDGE,"E11.3.0.0"),sQuery(id+"F0.wireOp",EDGE,"E11.3.0.1"),sQuery(id+"F0.wireOp",EDGE,"E11.3.0.3"),sQuery(id+"F0.wireOp",EDGE,"E11.4.0.0"),sQuery(id+"F0.wireOp",EDGE,"E11.4.0.1"),sQuery(id+"F0.wireOp",EDGE,"E11.4.0.3"),sQuery(id+"F0.wireOp",EDGE,"E11.5.0.0"),sQuery(id+"F0.wireOp",EDGE,"E11.5.0.1"),sQuery(id+"F0.wireOp",EDGE,"E11.5.0.3"),sQuery(id+"F0.wireOp",EDGE,"E11.6.0.0"),sQuery(id+"F0.wireOp",EDGE,"E11.6.0.1"),sQuery(id+"F0.wireOp",EDGE,"E11.6.0.3"),sQuery(id+"F0.wireOp",EDGE,"E11.7.0.0"),sQuery(id+"F0.wireOp",EDGE,"E11.7.0.1"),sQuery(id+"F0.wireOp",EDGE,"E11.7.0.3"),sQuery(id+"F0.wireOp",EDGE,"E11.8.0.0"),sQuery(id+"F0.wireOp",EDGE,"E11.8.0.1"),sQuery(id+"F0.wireOp",EDGE,"E11.8.0.3"),sQuery(id+"F0.wireOp",EDGE,"E11.9.0.0"),sQuery(id+"F0.wireOp",EDGE,"E11.9.0.3"),sQuery(id+"F0.wireOp",EDGE,"E11.2.0.2"),sQuery(id+"F0.wireOp",EDGE,"E11.3.0.2"),sQuery(id+"F0.wireOp",EDGE,"E11.4.0.2"),sQuery(id+"F0.wireOp",EDGE,"E11.5.0.2"),sQuery(id+"F0.wireOp",EDGE,"E11.6.0.2"),sQuery(id+"F0.wireOp",EDGE,"E11.7.0.2"),sQuery(id+"F0.wireOp",EDGE,"E11.8.0.2"),sQuery(id+"F0.wireOp",EDGE,"E11.9.0.2"),sQuery(id+"F0.wireOp",EDGE,"E13.0.2.2"),sQuery(id+"F0.wireOp",EDGE,"E13.0.3.1"),sQuery(id+"F0.wireOp",EDGE,"E13.0.3.2"),sQuery(id+"F0.wireOp",EDGE,"E13.0.3.3"),sQuery(id+"F0.wireOp",EDGE,"E13.0.4.1"),sQuery(id+"F0.wireOp",EDGE,"E13.0.4.2"),sQuery(id+"F0.wireOp",EDGE,"E13.0.4.3"),sQuery(id+"F0.wireOp",EDGE,"E14.trimOffspring"),sQuery(id+"F0.wireOp",EDGE,"E15.trimOffspring"),sQuery(id+"F0.wireOp",EDGE,"E16.trimOffspring"),sQuery(id+"F0.wireOp",EDGE,"E18.top"),sQuery(id+"F0.wireOp",EDGE,"E18.left"),sQuery(id+"F0.wireOp",EDGE,"E18.right"),sQuery(id+"F0.wireOp",EDGE,"E19.trimOffspring"),sQuery(id+"F0.wireOp",EDGE,"E20.1.0.0"),sQuery(id+"F0.wireOp",EDGE,"E20.1.0.1"),sQuery(id+"F0.wireOp",EDGE,"E20.1.0.2"),sQuery(id+"F0.wireOp",EDGE,"E20.2.0.0"),sQuery(id+"F0.wireOp",EDGE,"E20.2.0.1"),sQuery(id+"F0.wireOp",EDGE,"E20.2.0.2"),sQuery(id+"F0.wireOp",EDGE,"E20.3.0.0"),sQuery(id+"F0.wireOp",EDGE,"E20.3.0.1"),sQuery(id+"F0.wireOp",EDGE,"E20.3.0.2"),sQuery(id+"F0.wireOp",EDGE,"E20.4.0.0"),sQuery(id+"F0.wireOp",EDGE,"E20.4.0.1"),sQuery(id+"F0.wireOp",EDGE,"E20.4.0.2"),sQuery(id+"F0.wireOp",EDGE,"E21.trimOffspring"),sQuery(id+"F0.wireOp",EDGE,"E22.trimOffspring"),sQuery(id+"F0.wireOp",EDGE,"E23.trimOffspring")])]}),"instanceName":"1"});
            var Q4;
            Q4=makeQuery(id+"F15.opExtrude","SWEPT_BODY",BODY,{"disambiguationData":[OSD([sQuery(id+"F12.wireOp",EDGE,"E43.bottom"),sQuery(id+"F12.wireOp",EDGE,"E43.top"),sQuery(id+"F12.wireOp",EDGE,"E43.left"),sQuery(id+"F12.wireOp",EDGE,"E43.right")])]});
            booleanBodies(context, id + "F16", {"operationType" : BooleanOperationType.SUBTRACTION, "tools" : qUnion([Q0, Q1, Q2, Q3]), "targets" : qUnion([Q4]), "keepTools" : true});
        }
        {
            var Q0;
            Q0=makeQuery(id+"F6.opExtrude","SWEPT_BODY",BODY,{"disambiguationData":[OSD([sQuery(id+"F3.wireOp",EDGE,"E29.bottom"),sQuery(id+"F3.wireOp",EDGE,"E29.top"),sQuery(id+"F3.wireOp",EDGE,"E29.left"),sQuery(id+"F3.wireOp",EDGE,"E29.right"),sQuery(id+"F3.wireOp",EDGE,"E30.top"),sQuery(id+"F3.wireOp",EDGE,"E30.right"),sQuery(id+"F3.wireOp",EDGE,"E31.top"),sQuery(id+"F3.wireOp",EDGE,"E31.right"),sQuery(id+"F3.wireOp",EDGE,"E32.1.0.0"),sQuery(id+"F3.wireOp",EDGE,"E32.1.0.1"),sQuery(id+"F3.wireOp",EDGE,"E32.1.0.2"),sQuery(id+"F3.wireOp",EDGE,"E32.2.0.0"),sQuery(id+"F3.wireOp",EDGE,"E32.2.0.1"),sQuery(id+"F3.wireOp",EDGE,"E32.2.0.2"),sQuery(id+"F3.wireOp",EDGE,"E32.3.0.0"),sQuery(id+"F3.wireOp",EDGE,"E32.3.0.1"),sQuery(id+"F3.wireOp",EDGE,"E32.3.0.2"),sQuery(id+"F3.wireOp",EDGE,"E32.4.0.0"),sQuery(id+"F3.wireOp",EDGE,"E32.4.0.1"),sQuery(id+"F3.wireOp",EDGE,"E32.4.0.2"),sQuery(id+"F3.wireOp",EDGE,"E33.1.0.1"),sQuery(id+"F3.wireOp",EDGE,"E33.1.0.2"),sQuery(id+"F3.wireOp",EDGE,"E33.1.0.3"),sQuery(id+"F3.wireOp",EDGE,"E33.2.0.1"),sQuery(id+"F3.wireOp",EDGE,"E33.2.0.2"),sQuery(id+"F3.wireOp",EDGE,"E33.2.0.3"),sQuery(id+"F3.wireOp",EDGE,"E33.3.0.1"),sQuery(id+"F3.wireOp",EDGE,"E33.3.0.2"),sQuery(id+"F3.wireOp",EDGE,"E33.3.0.3"),sQuery(id+"F3.wireOp",EDGE,"E33.4.0.1"),sQuery(id+"F3.wireOp",EDGE,"E33.4.0.2"),sQuery(id+"F3.wireOp",EDGE,"E33.4.0.3"),sQuery(id+"F3.wireOp",EDGE,"E34.trimOffspring"),sQuery(id+"F3.wireOp",EDGE,"E35.trimOffspring"),sQuery(id+"F3.wireOp",EDGE,"E36.trimOffspring"),sQuery(id+"F3.wireOp",EDGE,"E37.trimOffspring"),sQuery(id+"F3.wireOp",EDGE,"E38.trimOffspring"),sQuery(id+"F3.wireOp",EDGE,"E39.trimOffspring"),sQuery(id+"F3.wireOp",EDGE,"E40.trimOffspring"),sQuery(id+"F3.wireOp",EDGE,"E41.trimOffspring")])]});
            var Q1;
            Q1=makeQuery(id+"F1.opExtrude","SWEPT_BODY",BODY,{"disambiguationData":[OSD([sQuery(id+"F0.wireOp",EDGE,"E0.bottom"),sQuery(id+"F0.wireOp",EDGE,"E0.top"),sQuery(id+"F0.wireOp",EDGE,"E0.left"),sQuery(id+"F0.wireOp",EDGE,"E1"),sQuery(id+"F0.wireOp",EDGE,"E2"),sQuery(id+"F0.wireOp",EDGE,"E3.bottom"),sQuery(id+"F0.wireOp",EDGE,"E3.top"),sQuery(id+"F0.wireOp",EDGE,"E3.right"),sQuery(id+"F0.wireOp",EDGE,"E4.trimOffspring"),sQuery(id+"F0.wireOp",EDGE,"E5.0.1.0"),sQuery(id+"F0.wireOp",EDGE,"E5.0.1.1"),sQuery(id+"F0.wireOp",EDGE,"E5.0.1.2"),sQuery(id+"F0.wireOp",EDGE,"E5.0.2.0"),sQuery(id+"F0.wireOp",EDGE,"E5.0.2.1"),sQuery(id+"F0.wireOp",EDGE,"E5.0.2.2"),sQuery(id+"F0.wireOp",EDGE,"E5.0.3.0"),sQuery(id+"F0.wireOp",EDGE,"E5.0.3.1"),sQuery(id+"F0.wireOp",EDGE,"E5.0.3.2"),sQuery(id+"F0.wireOp",EDGE,"E5.0.4.0"),sQuery(id+"F0.wireOp",EDGE,"E5.0.4.1"),sQuery(id+"F0.wireOp",EDGE,"E6.trimOffspring"),sQuery(id+"F0.wireOp",EDGE,"E7.trimOffspring"),sQuery(id+"F0.wireOp",EDGE,"E8.trimOffspring"),sQuery(id+"F0.wireOp",EDGE,"E9.top"),sQuery(id+"F0.wireOp",EDGE,"E9.left"),sQuery(id+"F0.wireOp",EDGE,"E9.right"),sQuery(id+"F0.wireOp",EDGE,"E11.1.0.0"),sQuery(id+"F0.wireOp",EDGE,"E11.1.0.1"),sQuery(id+"F0.wireOp",EDGE,"E10.trimOffspring"),sQuery(id+"F0.wireOp",EDGE,"E11.1.0.3"),sQuery(id+"F0.wireOp",EDGE,"E11.2.0.0"),sQuery(id+"F0.wireOp",EDGE,"E11.2.0.1"),sQuery(id+"F0.wireOp",EDGE,"E11.2.0.3"),sQuery(id+"F0.wireOp",EDGE,"E11.3.0.0"),sQuery(id+"F0.wireOp",EDGE,"E11.3.0.1"),sQuery(id+"F0.wireOp",EDGE,"E11.3.0.3"),sQuery(id+"F0.wireOp",EDGE,"E11.4.0.0"),sQuery(id+"F0.wireOp",EDGE,"E11.4.0.1"),sQuery(id+"F0.wireOp",EDGE,"E11.4.0.3"),sQuery(id+"F0.wireOp",EDGE,"E11.5.0.0"),sQuery(id+"F0.wireOp",EDGE,"E11.5.0.1"),sQuery(id+"F0.wireOp",EDGE,"E11.5.0.3"),sQuery(id+"F0.wireOp",EDGE,"E11.6.0.0"),sQuery(id+"F0.wireOp",EDGE,"E11.6.0.1"),sQuery(id+"F0.wireOp",EDGE,"E11.6.0.3"),sQuery(id+"F0.wireOp",EDGE,"E11.7.0.0"),sQuery(id+"F0.wireOp",EDGE,"E11.7.0.1"),sQuery(id+"F0.wireOp",EDGE,"E11.7.0.3"),sQuery(id+"F0.wireOp",EDGE,"E11.8.0.0"),sQuery(id+"F0.wireOp",EDGE,"E11.8.0.1"),sQuery(id+"F0.wireOp",EDGE,"E11.8.0.3"),sQuery(id+"F0.wireOp",EDGE,"E11.9.0.0"),sQuery(id+"F0.wireOp",EDGE,"E11.9.0.3"),sQuery(id+"F0.wireOp",EDGE,"E11.2.0.2"),sQuery(id+"F0.wireOp",EDGE,"E11.3.0.2"),sQuery(id+"F0.wireOp",EDGE,"E11.4.0.2"),sQuery(id+"F0.wireOp",EDGE,"E11.5.0.2"),sQuery(id+"F0.wireOp",EDGE,"E11.6.0.2"),sQuery(id+"F0.wireOp",EDGE,"E11.7.0.2"),sQuery(id+"F0.wireOp",EDGE,"E11.8.0.2"),sQuery(id+"F0.wireOp",EDGE,"E11.9.0.2"),sQuery(id+"F0.wireOp",EDGE,"E13.0.2.2"),sQuery(id+"F0.wireOp",EDGE,"E13.0.3.1"),sQuery(id+"F0.wireOp",EDGE,"E13.0.3.2"),sQuery(id+"F0.wireOp",EDGE,"E13.0.3.3"),sQuery(id+"F0.wireOp",EDGE,"E13.0.4.1"),sQuery(id+"F0.wireOp",EDGE,"E13.0.4.2"),sQuery(id+"F0.wireOp",EDGE,"E13.0.4.3"),sQuery(id+"F0.wireOp",EDGE,"E14.trimOffspring"),sQuery(id+"F0.wireOp",EDGE,"E15.trimOffspring"),sQuery(id+"F0.wireOp",EDGE,"E16.trimOffspring"),sQuery(id+"F0.wireOp",EDGE,"E18.top"),sQuery(id+"F0.wireOp",EDGE,"E18.left"),sQuery(id+"F0.wireOp",EDGE,"E18.right"),sQuery(id+"F0.wireOp",EDGE,"E19.trimOffspring"),sQuery(id+"F0.wireOp",EDGE,"E20.1.0.0"),sQuery(id+"F0.wireOp",EDGE,"E20.1.0.1"),sQuery(id+"F0.wireOp",EDGE,"E20.1.0.2"),sQuery(id+"F0.wireOp",EDGE,"E20.2.0.0"),sQuery(id+"F0.wireOp",EDGE,"E20.2.0.1"),sQuery(id+"F0.wireOp",EDGE,"E20.2.0.2"),sQuery(id+"F0.wireOp",EDGE,"E20.3.0.0"),sQuery(id+"F0.wireOp",EDGE,"E20.3.0.1"),sQuery(id+"F0.wireOp",EDGE,"E20.3.0.2"),sQuery(id+"F0.wireOp",EDGE,"E20.4.0.0"),sQuery(id+"F0.wireOp",EDGE,"E20.4.0.1"),sQuery(id+"F0.wireOp",EDGE,"E20.4.0.2"),sQuery(id+"F0.wireOp",EDGE,"E21.trimOffspring"),sQuery(id+"F0.wireOp",EDGE,"E22.trimOffspring"),sQuery(id+"F0.wireOp",EDGE,"E23.trimOffspring")])]});
            var Q2;
            Q2=makeQuery(id+"F4.opPattern","COPY",BODY,{"derivedFrom":makeQuery(id+"F1.opExtrude","SWEPT_BODY",BODY,{"disambiguationData":[OSD([sQuery(id+"F0.wireOp",EDGE,"E0.bottom"),sQuery(id+"F0.wireOp",EDGE,"E0.top"),sQuery(id+"F0.wireOp",EDGE,"E0.left"),sQuery(id+"F0.wireOp",EDGE,"E1"),sQuery(id+"F0.wireOp",EDGE,"E2"),sQuery(id+"F0.wireOp",EDGE,"E3.bottom"),sQuery(id+"F0.wireOp",EDGE,"E3.top"),sQuery(id+"F0.wireOp",EDGE,"E3.right"),sQuery(id+"F0.wireOp",EDGE,"E4.trimOffspring"),sQuery(id+"F0.wireOp",EDGE,"E5.0.1.0"),sQuery(id+"F0.wireOp",EDGE,"E5.0.1.1"),sQuery(id+"F0.wireOp",EDGE,"E5.0.1.2"),sQuery(id+"F0.wireOp",EDGE,"E5.0.2.0"),sQuery(id+"F0.wireOp",EDGE,"E5.0.2.1"),sQuery(id+"F0.wireOp",EDGE,"E5.0.2.2"),sQuery(id+"F0.wireOp",EDGE,"E5.0.3.0"),sQuery(id+"F0.wireOp",EDGE,"E5.0.3.1"),sQuery(id+"F0.wireOp",EDGE,"E5.0.3.2"),sQuery(id+"F0.wireOp",EDGE,"E5.0.4.0"),sQuery(id+"F0.wireOp",EDGE,"E5.0.4.1"),sQuery(id+"F0.wireOp",EDGE,"E6.trimOffspring"),sQuery(id+"F0.wireOp",EDGE,"E7.trimOffspring"),sQuery(id+"F0.wireOp",EDGE,"E8.trimOffspring"),sQuery(id+"F0.wireOp",EDGE,"E9.top"),sQuery(id+"F0.wireOp",EDGE,"E9.left"),sQuery(id+"F0.wireOp",EDGE,"E9.right"),sQuery(id+"F0.wireOp",EDGE,"E11.1.0.0"),sQuery(id+"F0.wireOp",EDGE,"E11.1.0.1"),sQuery(id+"F0.wireOp",EDGE,"E10.trimOffspring"),sQuery(id+"F0.wireOp",EDGE,"E11.1.0.3"),sQuery(id+"F0.wireOp",EDGE,"E11.2.0.0"),sQuery(id+"F0.wireOp",EDGE,"E11.2.0.1"),sQuery(id+"F0.wireOp",EDGE,"E11.2.0.3"),sQuery(id+"F0.wireOp",EDGE,"E11.3.0.0"),sQuery(id+"F0.wireOp",EDGE,"E11.3.0.1"),sQuery(id+"F0.wireOp",EDGE,"E11.3.0.3"),sQuery(id+"F0.wireOp",EDGE,"E11.4.0.0"),sQuery(id+"F0.wireOp",EDGE,"E11.4.0.1"),sQuery(id+"F0.wireOp",EDGE,"E11.4.0.3"),sQuery(id+"F0.wireOp",EDGE,"E11.5.0.0"),sQuery(id+"F0.wireOp",EDGE,"E11.5.0.1"),sQuery(id+"F0.wireOp",EDGE,"E11.5.0.3"),sQuery(id+"F0.wireOp",EDGE,"E11.6.0.0"),sQuery(id+"F0.wireOp",EDGE,"E11.6.0.1"),sQuery(id+"F0.wireOp",EDGE,"E11.6.0.3"),sQuery(id+"F0.wireOp",EDGE,"E11.7.0.0"),sQuery(id+"F0.wireOp",EDGE,"E11.7.0.1"),sQuery(id+"F0.wireOp",EDGE,"E11.7.0.3"),sQuery(id+"F0.wireOp",EDGE,"E11.8.0.0"),sQuery(id+"F0.wireOp",EDGE,"E11.8.0.1"),sQuery(id+"F0.wireOp",EDGE,"E11.8.0.3"),sQuery(id+"F0.wireOp",EDGE,"E11.9.0.0"),sQuery(id+"F0.wireOp",EDGE,"E11.9.0.3"),sQuery(id+"F0.wireOp",EDGE,"E11.2.0.2"),sQuery(id+"F0.wireOp",EDGE,"E11.3.0.2"),sQuery(id+"F0.wireOp",EDGE,"E11.4.0.2"),sQuery(id+"F0.wireOp",EDGE,"E11.5.0.2"),sQuery(id+"F0.wireOp",EDGE,"E11.6.0.2"),sQuery(id+"F0.wireOp",EDGE,"E11.7.0.2"),sQuery(id+"F0.wireOp",EDGE,"E11.8.0.2"),sQuery(id+"F0.wireOp",EDGE,"E11.9.0.2"),sQuery(id+"F0.wireOp",EDGE,"E13.0.2.2"),sQuery(id+"F0.wireOp",EDGE,"E13.0.3.1"),sQuery(id+"F0.wireOp",EDGE,"E13.0.3.2"),sQuery(id+"F0.wireOp",EDGE,"E13.0.3.3"),sQuery(id+"F0.wireOp",EDGE,"E13.0.4.1"),sQuery(id+"F0.wireOp",EDGE,"E13.0.4.2"),sQuery(id+"F0.wireOp",EDGE,"E13.0.4.3"),sQuery(id+"F0.wireOp",EDGE,"E14.trimOffspring"),sQuery(id+"F0.wireOp",EDGE,"E15.trimOffspring"),sQuery(id+"F0.wireOp",EDGE,"E16.trimOffspring"),sQuery(id+"F0.wireOp",EDGE,"E18.top"),sQuery(id+"F0.wireOp",EDGE,"E18.left"),sQuery(id+"F0.wireOp",EDGE,"E18.right"),sQuery(id+"F0.wireOp",EDGE,"E19.trimOffspring"),sQuery(id+"F0.wireOp",EDGE,"E20.1.0.0"),sQuery(id+"F0.wireOp",EDGE,"E20.1.0.1"),sQuery(id+"F0.wireOp",EDGE,"E20.1.0.2"),sQuery(id+"F0.wireOp",EDGE,"E20.2.0.0"),sQuery(id+"F0.wireOp",EDGE,"E20.2.0.1"),sQuery(id+"F0.wireOp",EDGE,"E20.2.0.2"),sQuery(id+"F0.wireOp",EDGE,"E20.3.0.0"),sQuery(id+"F0.wireOp",EDGE,"E20.3.0.1"),sQuery(id+"F0.wireOp",EDGE,"E20.3.0.2"),sQuery(id+"F0.wireOp",EDGE,"E20.4.0.0"),sQuery(id+"F0.wireOp",EDGE,"E20.4.0.1"),sQuery(id+"F0.wireOp",EDGE,"E20.4.0.2"),sQuery(id+"F0.wireOp",EDGE,"E21.trimOffspring"),sQuery(id+"F0.wireOp",EDGE,"E22.trimOffspring"),sQuery(id+"F0.wireOp",EDGE,"E23.trimOffspring")])]}),"instanceName":"1"});
            var Q3;
            Q3=makeQuery(id+"F13.opExtrude","SWEPT_BODY",BODY,{"disambiguationData":[OSD([sQuery(id+"F12.wireOp",EDGE,"E43.top"),sQuery(id+"F12.wireOp",EDGE,"E43.left"),sQuery(id+"F12.wireOp",EDGE,"E43.right"),sQuery(id+"F12.wireOp",EDGE,"E44")])]});
            booleanBodies(context, id + "F17", {"operationType" : BooleanOperationType.SUBTRACTION, "tools" : qUnion([Q0, Q1, Q2]), "targets" : qUnion([Q3]), "keepTools" : true});
        }
        {
            var Q0;
            Q0=makeQuery(id+"F2.opExtrude","SWEPT_BODY",BODY,{"disambiguationData":[OSD([sQuery(id+"F0.wireOp",EDGE,"E0.right"),sQuery(id+"F0.wireOp",EDGE,"E1"),sQuery(id+"F0.wireOp",EDGE,"E2"),sQuery(id+"F0.wireOp",EDGE,"E12.top"),sQuery(id+"F0.wireOp",EDGE,"E12.left"),sQuery(id+"F0.wireOp",EDGE,"E13.0.1.1"),sQuery(id+"F0.wireOp",EDGE,"E13.0.1.2"),sQuery(id+"F0.wireOp",EDGE,"E13.0.1.3"),sQuery(id+"F0.wireOp",EDGE,"E13.0.2.1"),sQuery(id+"F0.wireOp",EDGE,"E13.0.2.3"),sQuery(id+"F0.wireOp",EDGE,"E17.trimOffspring"),sQuery(id+"F0.wireOp",EDGE,"E20.5.0.0"),sQuery(id+"F0.wireOp",EDGE,"E20.5.0.1"),sQuery(id+"F0.wireOp",EDGE,"E20.5.0.2"),sQuery(id+"F0.wireOp",EDGE,"E20.6.0.0"),sQuery(id+"F0.wireOp",EDGE,"E20.6.0.1"),sQuery(id+"F0.wireOp",EDGE,"E20.6.0.2"),sQuery(id+"F0.wireOp",EDGE,"E20.7.0.0"),sQuery(id+"F0.wireOp",EDGE,"E20.7.0.1"),sQuery(id+"F0.wireOp",EDGE,"E20.7.0.2"),sQuery(id+"F0.wireOp",EDGE,"E20.8.0.0"),sQuery(id+"F0.wireOp",EDGE,"E20.8.0.1"),sQuery(id+"F0.wireOp",EDGE,"E20.8.0.2"),sQuery(id+"F0.wireOp",EDGE,"E20.9.0.0"),sQuery(id+"F0.wireOp",EDGE,"E20.9.0.2"),sQuery(id+"F0.wireOp",EDGE,"E24.trimOffspring"),sQuery(id+"F0.wireOp",EDGE,"E25.trimOffspring"),sQuery(id+"F0.wireOp",EDGE,"E26.trimOffspring"),sQuery(id+"F0.wireOp",EDGE,"E27.trimOffspring"),sQuery(id+"F0.wireOp",EDGE,"E28.trimOffspring")])]});
            var Q1;
            Q1=makeQuery(id+"F9.opExtrude","SWEPT_BODY",BODY,{"disambiguationData":[OSD([sQuery(id+"F3.wireOp",EDGE,"E29.bottom"),sQuery(id+"F3.wireOp",EDGE,"E29.left"),sQuery(id+"F3.wireOp",EDGE,"E29.right"),sQuery(id+"F3.wireOp",EDGE,"E30.top"),sQuery(id+"F3.wireOp",EDGE,"E30.right"),sQuery(id+"F3.wireOp",EDGE,"E32.1.0.0"),sQuery(id+"F3.wireOp",EDGE,"E32.1.0.1"),sQuery(id+"F3.wireOp",EDGE,"E32.1.0.2"),sQuery(id+"F3.wireOp",EDGE,"E32.2.0.0"),sQuery(id+"F3.wireOp",EDGE,"E32.2.0.1"),sQuery(id+"F3.wireOp",EDGE,"E32.2.0.2"),sQuery(id+"F3.wireOp",EDGE,"E32.3.0.0"),sQuery(id+"F3.wireOp",EDGE,"E32.3.0.1"),sQuery(id+"F3.wireOp",EDGE,"E32.3.0.2"),sQuery(id+"F3.wireOp",EDGE,"E32.4.0.0"),sQuery(id+"F3.wireOp",EDGE,"E32.4.0.1"),sQuery(id+"F3.wireOp",EDGE,"E32.4.0.2"),sQuery(id+"F3.wireOp",EDGE,"E34.trimOffspring"),sQuery(id+"F3.wireOp",EDGE,"E35.trimOffspring"),sQuery(id+"F3.wireOp",EDGE,"E36.trimOffspring"),sQuery(id+"F3.wireOp",EDGE,"E37.trimOffspring"),sQuery(id+"F3.wireOp",EDGE,"E42")])]});
            var Q2;
            Q2=makeQuery(id+"F5.opPattern","COPY",BODY,{"derivedFrom":makeQuery(id+"F2.opExtrude","SWEPT_BODY",BODY,{"disambiguationData":[OSD([sQuery(id+"F0.wireOp",EDGE,"E0.right"),sQuery(id+"F0.wireOp",EDGE,"E1"),sQuery(id+"F0.wireOp",EDGE,"E2"),sQuery(id+"F0.wireOp",EDGE,"E12.top"),sQuery(id+"F0.wireOp",EDGE,"E12.left"),sQuery(id+"F0.wireOp",EDGE,"E13.0.1.1"),sQuery(id+"F0.wireOp",EDGE,"E13.0.1.2"),sQuery(id+"F0.wireOp",EDGE,"E13.0.1.3"),sQuery(id+"F0.wireOp",EDGE,"E13.0.2.1"),sQuery(id+"F0.wireOp",EDGE,"E13.0.2.3"),sQuery(id+"F0.wireOp",EDGE,"E17.trimOffspring"),sQuery(id+"F0.wireOp",EDGE,"E20.5.0.0"),sQuery(id+"F0.wireOp",EDGE,"E20.5.0.1"),sQuery(id+"F0.wireOp",EDGE,"E20.5.0.2"),sQuery(id+"F0.wireOp",EDGE,"E20.6.0.0"),sQuery(id+"F0.wireOp",EDGE,"E20.6.0.1"),sQuery(id+"F0.wireOp",EDGE,"E20.6.0.2"),sQuery(id+"F0.wireOp",EDGE,"E20.7.0.0"),sQuery(id+"F0.wireOp",EDGE,"E20.7.0.1"),sQuery(id+"F0.wireOp",EDGE,"E20.7.0.2"),sQuery(id+"F0.wireOp",EDGE,"E20.8.0.0"),sQuery(id+"F0.wireOp",EDGE,"E20.8.0.1"),sQuery(id+"F0.wireOp",EDGE,"E20.8.0.2"),sQuery(id+"F0.wireOp",EDGE,"E20.9.0.0"),sQuery(id+"F0.wireOp",EDGE,"E20.9.0.2"),sQuery(id+"F0.wireOp",EDGE,"E24.trimOffspring"),sQuery(id+"F0.wireOp",EDGE,"E25.trimOffspring"),sQuery(id+"F0.wireOp",EDGE,"E26.trimOffspring"),sQuery(id+"F0.wireOp",EDGE,"E27.trimOffspring"),sQuery(id+"F0.wireOp",EDGE,"E28.trimOffspring")])]}),"instanceName":"1"});
            var Q3;
            Q3=makeQuery(id+"F14.opExtrude","SWEPT_BODY",BODY,{"disambiguationData":[OSD([sQuery(id+"F12.wireOp",EDGE,"E43.bottom"),sQuery(id+"F12.wireOp",EDGE,"E43.left"),sQuery(id+"F12.wireOp",EDGE,"E43.right"),sQuery(id+"F12.wireOp",EDGE,"E44")])]});
            booleanBodies(context, id + "F18", {"operationType" : BooleanOperationType.SUBTRACTION, "tools" : qUnion([Q0, Q1, Q2]), "targets" : qUnion([Q3]), "keepTools" : true});
        }
    });
